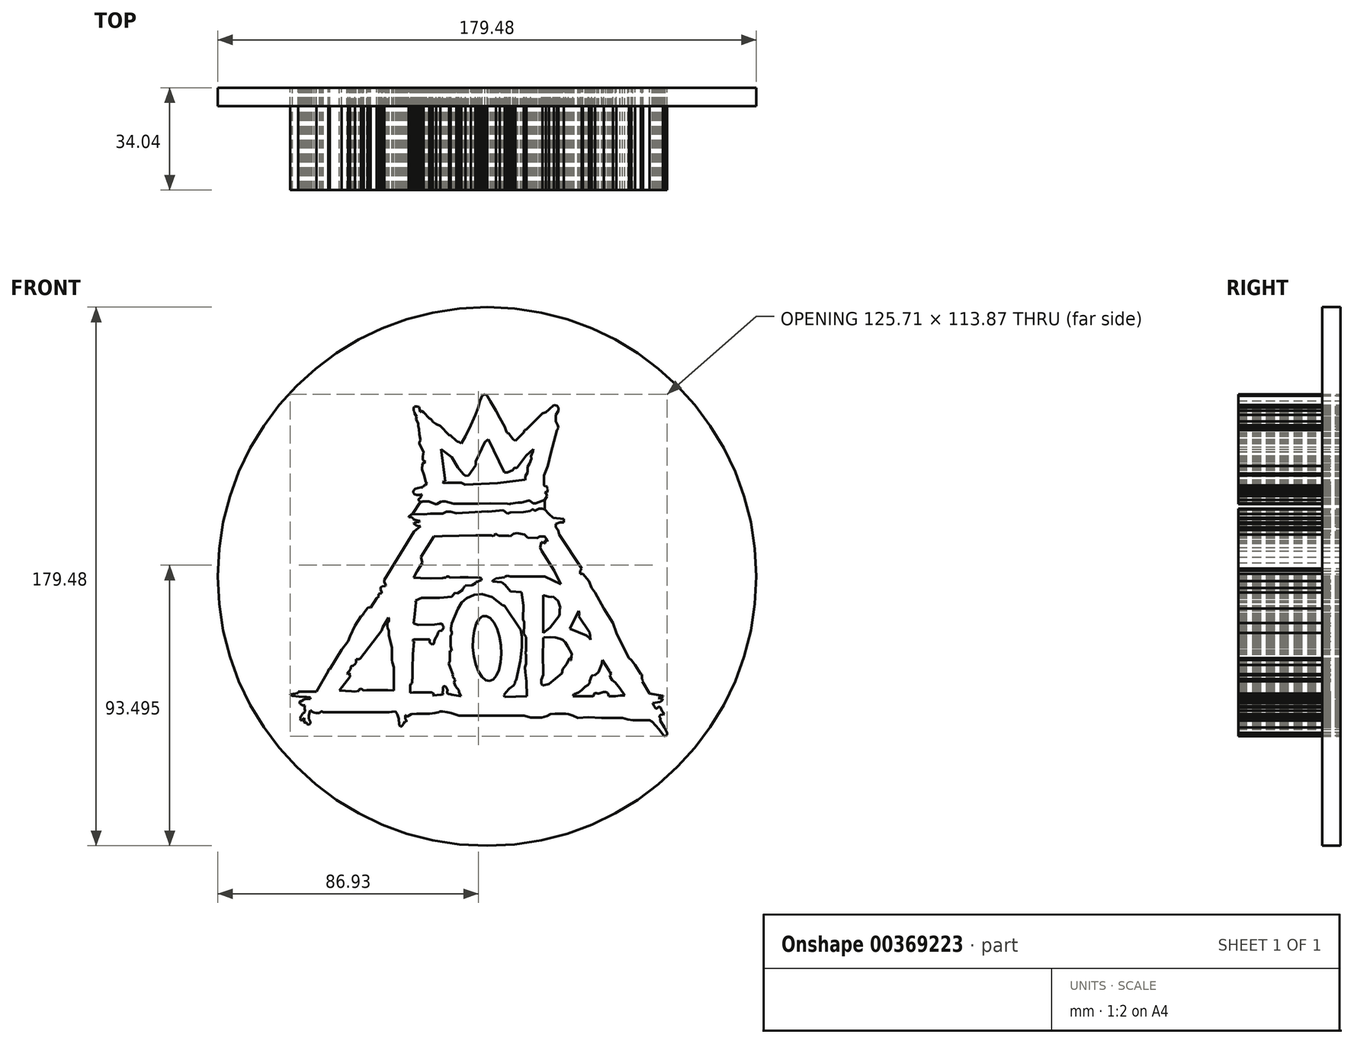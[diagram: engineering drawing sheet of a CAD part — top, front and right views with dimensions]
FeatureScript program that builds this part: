
annotation { "Feature Type Name" : "Feature", "Feature Type Description" : "" }
export const myFeature = defineFeature(function(context is Context, id is Id, definition is map)
    precondition{}
    {
        {
            var Q0;
            Q0=qCreatedBy(makeId("Front.planeOp"),FACE);
            var sketch = newSketch(context, id + "F0", { "sketchPlane" : qUnion([Q0])});
            skLineSegment(sketch, "E0", {"start": v(-62.94, -38.4) * mm, "end": v(-62.94, -38.9) * mm});
            skLineSegment(sketch, "E1", {"start": v(-62.94, -38.9) * mm, "end": v(-65.66, -39.21) * mm});
            skLineSegment(sketch, "E2", {"start": v(-65.66, -39.21) * mm, "end": v(-65.66, -39.45) * mm});
            skLineSegment(sketch, "E3", {"start": v(-65.66, -39.45) * mm, "end": v(-64.85, -39.72) * mm});
            skLineSegment(sketch, "E4", {"start": v(-64.85, -39.72) * mm, "end": v(-62.67, -39.97) * mm});
            skLineSegment(sketch, "E5", {"start": v(-62.67, -39.97) * mm, "end": v(-60.13, -40.15) * mm});
            skLineSegment(sketch, "E6", {"start": v(-60.13, -40.15) * mm, "end": v(-59.1, -40.28) * mm});
            skLineSegment(sketch, "E7", {"start": v(-59.1, -40.28) * mm, "end": v(-58.84, -40.47) * mm});
            skLineSegment(sketch, "E8", {"start": v(-58.84, -40.47) * mm, "end": v(-58.84, -40.74) * mm});
            skLineSegment(sketch, "E9", {"start": v(-58.84, -40.74) * mm, "end": v(-59.6, -40.74) * mm});
            skLineSegment(sketch, "E10", {"start": v(-59.6, -40.74) * mm, "end": v(-60.49, -40.74) * mm});
            skLineSegment(sketch, "E11", {"start": v(-60.49, -40.74) * mm, "end": v(-61.46, -41.23) * mm});
            skLineSegment(sketch, "E12", {"start": v(-61.46, -41.23) * mm, "end": v(-61.58, -41.33) * mm});
            skLineSegment(sketch, "E13", {"start": v(-61.58, -41.33) * mm, "end": v(-61.58, -41.7) * mm});
            skLineSegment(sketch, "E14", {"start": v(-61.58, -41.7) * mm, "end": v(-61.93, -41.55) * mm});
            skLineSegment(sketch, "E15", {"start": v(-61.93, -41.55) * mm, "end": v(-62.35, -41.55) * mm});
            skLineSegment(sketch, "E16", {"start": v(-62.35, -41.55) * mm, "end": v(-62.46, -41.71) * mm});
            skLineSegment(sketch, "E17", {"start": v(-62.46, -41.71) * mm, "end": v(-62.46, -42.04) * mm});
            skLineSegment(sketch, "E18", {"start": v(-62.46, -42.04) * mm, "end": v(-62.35, -42.44) * mm});
            skLineSegment(sketch, "E19", {"start": v(-62.35, -42.44) * mm, "end": v(-61.46, -42.92) * mm});
            skLineSegment(sketch, "E20", {"start": v(-61.46, -42.92) * mm, "end": v(-60.65, -42.92) * mm});
            skLineSegment(sketch, "E21", {"start": v(-60.65, -42.92) * mm, "end": v(-60.75, -43.15) * mm});
            skLineSegment(sketch, "E22", {"start": v(-60.75, -43.15) * mm, "end": v(-60.83, -43.5) * mm});
            skLineSegment(sketch, "E23", {"start": v(-60.83, -43.5) * mm, "end": v(-60.83, -43.8) * mm});
            skLineSegment(sketch, "E24", {"start": v(-60.83, -43.8) * mm, "end": v(-60.72, -44.25) * mm});
            skLineSegment(sketch, "E25", {"start": v(-60.72, -44.25) * mm, "end": v(-60.6, -44.61) * mm});
            skLineSegment(sketch, "E26", {"start": v(-60.6, -44.61) * mm, "end": v(-60.6, -45.04) * mm});
            skLineSegment(sketch, "E27", {"start": v(-60.6, -45.04) * mm, "end": v(-60.94, -45.41) * mm});
            skLineSegment(sketch, "E28", {"start": v(-60.94, -45.41) * mm, "end": v(-61.39, -45.64) * mm});
            skLineSegment(sketch, "E29", {"start": v(-61.39, -45.64) * mm, "end": v(-61.52, -45.82) * mm});
            skLineSegment(sketch, "E30", {"start": v(-61.52, -45.82) * mm, "end": v(-61.6, -46) * mm});
            skLineSegment(sketch, "E31", {"start": v(-61.6, -46) * mm, "end": v(-61.65, -46.18) * mm});
            skLineSegment(sketch, "E32", {"start": v(-61.65, -46.18) * mm, "end": v(-61.81, -46.37) * mm});
            skLineSegment(sketch, "E33", {"start": v(-61.81, -46.37) * mm, "end": v(-62.03, -46.6) * mm});
            skLineSegment(sketch, "E34", {"start": v(-62.03, -46.6) * mm, "end": v(-62.14, -46.84) * mm});
            skLineSegment(sketch, "E35", {"start": v(-62.14, -46.84) * mm, "end": v(-62.14, -47.19) * mm});
            skLineSegment(sketch, "E36", {"start": v(-62.14, -47.19) * mm, "end": v(-62.03, -47.35) * mm});
            skLineSegment(sketch, "E37", {"start": v(-62.03, -47.35) * mm, "end": v(-62.14, -47.67) * mm});
            skLineSegment(sketch, "E38", {"start": v(-62.14, -47.67) * mm, "end": v(-62.14, -47.89) * mm});
            skLineSegment(sketch, "E39", {"start": v(-62.14, -47.89) * mm, "end": v(-61.9, -47.89) * mm});
            skLineSegment(sketch, "E40", {"start": v(-61.9, -47.89) * mm, "end": v(-61.39, -47.6) * mm});
            skLineSegment(sketch, "E41", {"start": v(-61.39, -47.6) * mm, "end": v(-60.97, -47.26) * mm});
            skLineSegment(sketch, "E42", {"start": v(-60.97, -47.26) * mm, "end": v(-60.85, -47.11) * mm});
            skLineSegment(sketch, "E43", {"start": v(-60.85, -47.11) * mm, "end": v(-60.85, -47.7) * mm});
            skLineSegment(sketch, "E44", {"start": v(-60.85, -47.7) * mm, "end": v(-60.98, -48.51) * mm});
            skLineSegment(sketch, "E45", {"start": v(-60.98, -48.51) * mm, "end": v(-60.74, -48.71) * mm});
            skLineSegment(sketch, "E46", {"start": v(-60.74, -48.71) * mm, "end": v(-60.44, -48.71) * mm});
            skLineSegment(sketch, "E47", {"start": v(-60.44, -48.71) * mm, "end": v(-60.44, -48.57) * mm});
            skLineSegment(sketch, "E48", {"start": v(-60.44, -48.57) * mm, "end": v(-60.32, -48.57) * mm});
            skLineSegment(sketch, "E49", {"start": v(-60.32, -48.57) * mm, "end": v(-60.01, -49.24) * mm});
            skLineSegment(sketch, "E50", {"start": v(-60.01, -49.24) * mm, "end": v(-59.44, -49.41) * mm});
            skLineSegment(sketch, "E51", {"start": v(-59.44, -49.41) * mm, "end": v(-59, -49.1) * mm});
            skLineSegment(sketch, "E52", {"start": v(-59, -49.1) * mm, "end": v(-58.85, -48.77) * mm});
            skLineSegment(sketch, "E53", {"start": v(-58.85, -48.77) * mm, "end": v(-58.85, -48.24) * mm});
            skLineSegment(sketch, "E54", {"start": v(-58.85, -48.24) * mm, "end": v(-59.08, -47.96) * mm});
            skLineSegment(sketch, "E55", {"start": v(-59.08, -47.96) * mm, "end": v(-59.35, -47.81) * mm});
            skLineSegment(sketch, "E56", {"start": v(-59.35, -47.81) * mm, "end": v(-59.48, -47.81) * mm});
            skLineSegment(sketch, "E57", {"start": v(-59.48, -47.81) * mm, "end": v(-59.24, -47.6) * mm});
            skLineSegment(sketch, "E58", {"start": v(-59.24, -47.6) * mm, "end": v(-59.35, -47.47) * mm});
            skLineSegment(sketch, "E59", {"start": v(-59.35, -47.47) * mm, "end": v(-59.35, -46.25) * mm});
            skLineSegment(sketch, "E60", {"start": v(-59.35, -46.25) * mm, "end": v(-59.06, -44.8) * mm});
            skLineSegment(sketch, "E61", {"start": v(-59.06, -44.8) * mm, "end": v(-58.85, -44.6) * mm});
            skLineSegment(sketch, "E62", {"start": v(-58.85, -44.6) * mm, "end": v(-58.63, -44.67) * mm});
            skLineSegment(sketch, "E63", {"start": v(-58.63, -44.67) * mm, "end": v(-58.51, -44.86) * mm});
            skLineSegment(sketch, "E64", {"start": v(-58.51, -44.86) * mm, "end": v(-58.2, -45.08) * mm});
            skLineSegment(sketch, "E65", {"start": v(-58.2, -45.08) * mm, "end": v(-57.6, -45.35) * mm});
            skLineSegment(sketch, "E66", {"start": v(-57.6, -45.35) * mm, "end": v(-56.98, -45.51) * mm});
            skLineSegment(sketch, "E67", {"start": v(-56.98, -45.51) * mm, "end": v(-55.88, -45.44) * mm});
            skLineSegment(sketch, "E68", {"start": v(-55.88, -45.44) * mm, "end": v(-55.28, -44.98) * mm});
            skLineSegment(sketch, "E69", {"start": v(-55.28, -44.98) * mm, "end": v(-55, -44.98) * mm});
            skLineSegment(sketch, "E70", {"start": v(-55, -44.98) * mm, "end": v(-54.58, -45.26) * mm});
            skLineSegment(sketch, "E71", {"start": v(-54.58, -45.26) * mm, "end": v(-53.2, -45.26) * mm});
            skLineSegment(sketch, "E72", {"start": v(-53.2, -45.26) * mm, "end": v(-42.52, -45.26) * mm});
            skLineSegment(sketch, "E73", {"start": v(-42.52, -45.26) * mm, "end": v(-41.83, -45.26) * mm});
            skLineSegment(sketch, "E74", {"start": v(-41.83, -45.26) * mm, "end": v(-38.86, -45.26) * mm});
            skLineSegment(sketch, "E75", {"start": v(-38.86, -45.26) * mm, "end": v(-33.5, -45.26) * mm});
            skLineSegment(sketch, "E76", {"start": v(-33.5, -45.26) * mm, "end": v(-32.63, -45.26) * mm});
            skLineSegment(sketch, "E77", {"start": v(-32.63, -45.26) * mm, "end": v(-31.71, -45.08) * mm});
            skLineSegment(sketch, "E78", {"start": v(-31.71, -45.08) * mm, "end": v(-31.05, -44.98) * mm});
            skLineSegment(sketch, "E79", {"start": v(-31.05, -44.98) * mm, "end": v(-30.44, -45.08) * mm});
            skLineSegment(sketch, "E80", {"start": v(-30.44, -45.08) * mm, "end": v(-29.9, -45.89) * mm});
            skLineSegment(sketch, "E81", {"start": v(-29.9, -45.89) * mm, "end": v(-29.4, -47.44) * mm});
            skLineSegment(sketch, "E82", {"start": v(-29.4, -47.44) * mm, "end": v(-29.22, -49.27) * mm});
            skLineSegment(sketch, "E83", {"start": v(-29.22, -49.27) * mm, "end": v(-28.87, -50.01) * mm});
            skLineSegment(sketch, "E84", {"start": v(-28.87, -50.01) * mm, "end": v(-28.5, -49.91) * mm});
            skLineSegment(sketch, "E85", {"start": v(-28.5, -49.91) * mm, "end": v(-28.17, -49.53) * mm});
            skLineSegment(sketch, "E86", {"start": v(-28.17, -49.53) * mm, "end": v(-27.91, -49.13) * mm});
            skLineSegment(sketch, "E87", {"start": v(-27.91, -49.13) * mm, "end": v(-27.4, -48.24) * mm});
            skLineSegment(sketch, "E88", {"start": v(-27.4, -48.24) * mm, "end": v(-27.1, -48.24) * mm});
            skLineSegment(sketch, "E89", {"start": v(-27.1, -48.24) * mm, "end": v(-26.93, -48.42) * mm});
            skLineSegment(sketch, "E90", {"start": v(-26.93, -48.42) * mm, "end": v(-26.93, -47.92) * mm});
            skLineSegment(sketch, "E91", {"start": v(-26.93, -47.92) * mm, "end": v(-27.27, -47.5) * mm});
            skLineSegment(sketch, "E92", {"start": v(-27.27, -47.5) * mm, "end": v(-27.27, -46.32) * mm});
            skLineSegment(sketch, "E93", {"start": v(-27.27, -46.32) * mm, "end": v(-27.09, -46.32) * mm});
            skLineSegment(sketch, "E94", {"start": v(-27.09, -46.32) * mm, "end": v(-26.73, -46.6) * mm});
            skLineSegment(sketch, "E95", {"start": v(-26.73, -46.6) * mm, "end": v(-26.48, -46.6) * mm});
            skLineSegment(sketch, "E96", {"start": v(-26.48, -46.6) * mm, "end": v(-25.24, -45.85) * mm});
            skLineSegment(sketch, "E97", {"start": v(-25.24, -45.85) * mm, "end": v(-23.42, -45.69) * mm});
            skLineSegment(sketch, "E98", {"start": v(-23.42, -45.69) * mm, "end": v(-19.14, -45.69) * mm});
            skLineSegment(sketch, "E99", {"start": v(-19.14, -45.69) * mm, "end": v(-17.32, -45.46) * mm});
            skLineSegment(sketch, "E100", {"start": v(-17.32, -45.46) * mm, "end": v(-16.12, -45.3) * mm});
            skLineSegment(sketch, "E101", {"start": v(-16.12, -45.3) * mm, "end": v(-15.95, -45.18) * mm});
            skLineSegment(sketch, "E102", {"start": v(-15.95, -45.18) * mm, "end": v(-15.87, -45.02) * mm});
            skLineSegment(sketch, "E103", {"start": v(-15.87, -45.02) * mm, "end": v(-14.84, -45.02) * mm});
            skLineSegment(sketch, "E104", {"start": v(-14.84, -45.02) * mm, "end": v(-13.3, -45.24) * mm});
            skLineSegment(sketch, "E105", {"start": v(-13.3, -45.24) * mm, "end": v(-11.96, -45.46) * mm});
            skLineSegment(sketch, "E106", {"start": v(-11.96, -45.46) * mm, "end": v(-9.28, -46.4) * mm});
            skLineSegment(sketch, "E107", {"start": v(-9.28, -46.4) * mm, "end": v(-2.03, -46.4) * mm});
            skLineSegment(sketch, "E108", {"start": v(-2.03, -46.4) * mm, "end": v(12.34, -46.4) * mm});
            skLineSegment(sketch, "E109", {"start": v(12.34, -46.4) * mm, "end": v(14.52, -47.04) * mm});
            skLineSegment(sketch, "E110", {"start": v(14.52, -47.04) * mm, "end": v(18.18, -47.04) * mm});
            skLineSegment(sketch, "E111", {"start": v(18.18, -47.04) * mm, "end": v(20, -46.46) * mm});
            skLineSegment(sketch, "E112", {"start": v(20, -46.46) * mm, "end": v(21.2, -45.92) * mm});
            skLineSegment(sketch, "E113", {"start": v(21.2, -45.92) * mm, "end": v(22.7, -45.8) * mm});
            skLineSegment(sketch, "E114", {"start": v(22.7, -45.8) * mm, "end": v(26.26, -45.8) * mm});
            skLineSegment(sketch, "E115", {"start": v(26.26, -45.8) * mm, "end": v(27.11, -45.9) * mm});
            skLineSegment(sketch, "E116", {"start": v(27.11, -45.9) * mm, "end": v(28.61, -46.41) * mm});
            skLineSegment(sketch, "E117", {"start": v(28.61, -46.41) * mm, "end": v(30.22, -47.11) * mm});
            skLineSegment(sketch, "E118", {"start": v(30.22, -47.11) * mm, "end": v(33.7, -46.91) * mm});
            skLineSegment(sketch, "E119", {"start": v(33.7, -46.91) * mm, "end": v(38.12, -47.15) * mm});
            skLineSegment(sketch, "E120", {"start": v(38.12, -47.15) * mm, "end": v(45.11, -47.15) * mm});
            skLineSegment(sketch, "E121", {"start": v(45.11, -47.15) * mm, "end": v(46.95, -47.7) * mm});
            skLineSegment(sketch, "E122", {"start": v(46.95, -47.7) * mm, "end": v(48.53, -47.9) * mm});
            skLineSegment(sketch, "E123", {"start": v(48.53, -47.9) * mm, "end": v(54.18, -47.9) * mm});
            skLineSegment(sketch, "E124", {"start": v(54.18, -47.9) * mm, "end": v(55.04, -48.36) * mm});
            skLineSegment(sketch, "E125", {"start": v(55.04, -48.36) * mm, "end": v(57.38, -50.9) * mm});
            skLineSegment(sketch, "E126", {"start": v(57.38, -50.9) * mm, "end": v(57.92, -51.84) * mm});
            skLineSegment(sketch, "E127", {"start": v(57.92, -51.84) * mm, "end": v(58.9, -52.94) * mm});
            skLineSegment(sketch, "E128", {"start": v(58.9, -52.94) * mm, "end": v(59.36, -53.18) * mm});
            skLineSegment(sketch, "E129", {"start": v(59.36, -53.18) * mm, "end": v(60.04, -52.8) * mm});
            skLineSegment(sketch, "E130", {"start": v(60.04, -52.8) * mm, "end": v(60.04, -52.11) * mm});
            skLineSegment(sketch, "E131", {"start": v(60.04, -52.11) * mm, "end": v(59.17, -50.3) * mm});
            skLineSegment(sketch, "E132", {"start": v(59.17, -50.3) * mm, "end": v(57.75, -48.03) * mm});
            skLineSegment(sketch, "E133", {"start": v(57.75, -48.03) * mm, "end": v(57.75, -47.62) * mm});
            skLineSegment(sketch, "E134", {"start": v(57.75, -47.62) * mm, "end": v(57.83, -47.43) * mm});
            skLineSegment(sketch, "E135", {"start": v(57.83, -47.43) * mm, "end": v(57.83, -47.3) * mm});
            skLineSegment(sketch, "E136", {"start": v(57.83, -47.3) * mm, "end": v(57.74, -47.16) * mm});
            skLineSegment(sketch, "E137", {"start": v(57.74, -47.16) * mm, "end": v(57.47, -46.86) * mm});
            skLineSegment(sketch, "E138", {"start": v(57.47, -46.86) * mm, "end": v(57.47, -46.52) * mm});
            skLineSegment(sketch, "E139", {"start": v(57.47, -46.52) * mm, "end": v(57.9, -46.13) * mm});
            skLineSegment(sketch, "E140", {"start": v(57.9, -46.13) * mm, "end": v(59.09, -45.92) * mm});
            skLineSegment(sketch, "E141", {"start": v(59.09, -45.92) * mm, "end": v(58.22, -44.78) * mm});
            skLineSegment(sketch, "E142", {"start": v(58.22, -44.78) * mm, "end": v(57.83, -43.73) * mm});
            skLineSegment(sketch, "E143", {"start": v(57.83, -43.73) * mm, "end": v(57.6, -43.49) * mm});
            skLineSegment(sketch, "E144", {"start": v(57.6, -43.49) * mm, "end": v(57.09, -43.49) * mm});
            skLineSegment(sketch, "E145", {"start": v(57.09, -43.49) * mm, "end": v(56.64, -44) * mm});
            skLineSegment(sketch, "E146", {"start": v(56.64, -44) * mm, "end": v(56.24, -44) * mm});
            skLineSegment(sketch, "E147", {"start": v(56.24, -44) * mm, "end": v(55.7, -43.15) * mm});
            skLineSegment(sketch, "E148", {"start": v(55.7, -43.15) * mm, "end": v(55.2, -42.16) * mm});
            skLineSegment(sketch, "E149", {"start": v(55.2, -42.16) * mm, "end": v(57.74, -41.85) * mm});
            skLineSegment(sketch, "E150", {"start": v(57.74, -41.85) * mm, "end": v(58.51, -41.14) * mm});
            skLineSegment(sketch, "E151", {"start": v(58.51, -41.14) * mm, "end": v(58.51, -40.76) * mm});
            skLineSegment(sketch, "E152", {"start": v(58.51, -40.76) * mm, "end": v(57.09, -40.55) * mm});
            skLineSegment(sketch, "E153", {"start": v(57.09, -40.55) * mm, "end": v(58.7, -40.06) * mm});
            skLineSegment(sketch, "E154", {"start": v(58.7, -40.06) * mm, "end": v(58.62, -39.83) * mm});
            skLineSegment(sketch, "E155", {"start": v(58.62, -39.83) * mm, "end": v(54.18, -39.01) * mm});
            skLineSegment(sketch, "E156", {"start": v(54.18, -39.01) * mm, "end": v(51.7, -34.97) * mm});
            skLineSegment(sketch, "E157", {"start": v(51.7, -34.97) * mm, "end": v(52.02, -34.68) * mm});
            skLineSegment(sketch, "E158", {"start": v(52.02, -34.68) * mm, "end": v(51.6, -34.22) * mm});
            skLineSegment(sketch, "E159", {"start": v(51.6, -34.22) * mm, "end": v(51.6, -32.89) * mm});
            skLineSegment(sketch, "E160", {"start": v(51.6, -32.89) * mm, "end": v(51.63, -32.62) * mm});
            skLineSegment(sketch, "E161", {"start": v(51.63, -32.62) * mm, "end": v(51.23, -32.56) * mm});
            skLineSegment(sketch, "E162", {"start": v(51.23, -32.56) * mm, "end": v(49.34, -29.48) * mm});
            skLineSegment(sketch, "E163", {"start": v(49.34, -29.48) * mm, "end": v(48.07, -27.83) * mm});
            skLineSegment(sketch, "E164", {"start": v(48.07, -27.83) * mm, "end": v(47.35, -27.22) * mm});
            skLineSegment(sketch, "E165", {"start": v(47.35, -27.22) * mm, "end": v(45.83, -24.27) * mm});
            skLineSegment(sketch, "E166", {"start": v(45.83, -24.27) * mm, "end": v(43.05, -18.86) * mm});
            skLineSegment(sketch, "E167", {"start": v(43.05, -18.86) * mm, "end": v(41.96, -15.47) * mm});
            skLineSegment(sketch, "E168", {"start": v(41.96, -15.47) * mm, "end": v(38.94, -10.75) * mm});
            skLineSegment(sketch, "E169", {"start": v(38.94, -10.75) * mm, "end": v(35.97, -5.36) * mm});
            skLineSegment(sketch, "E170", {"start": v(35.97, -5.36) * mm, "end": v(34.88, -3.8) * mm});
            skLineSegment(sketch, "E171", {"start": v(34.88, -3.8) * mm, "end": v(33.91, -1.5) * mm});
            skLineSegment(sketch, "E172", {"start": v(33.91, -1.5) * mm, "end": v(31.98, 0.87) * mm});
            skLineSegment(sketch, "E173", {"start": v(31.98, 0.87) * mm, "end": v(31, 0.87) * mm});
            skLineSegment(sketch, "E174", {"start": v(31, 0.87) * mm, "end": v(31, 1.84) * mm});
            skLineSegment(sketch, "E175", {"start": v(31, 1.84) * mm, "end": v(31.55, 2.62) * mm});
            skLineSegment(sketch, "E176", {"start": v(31.55, 2.62) * mm, "end": v(24.1, 13.9) * mm});
            skLineSegment(sketch, "E177", {"start": v(24.1, 13.9) * mm, "end": v(23.67, 15.48) * mm});
            skLineSegment(sketch, "E178", {"start": v(23.67, 15.48) * mm, "end": v(22.9, 16.38) * mm});
            skLineSegment(sketch, "E179", {"start": v(22.9, 16.38) * mm, "end": v(22.9, 17.5) * mm});
            skLineSegment(sketch, "E180", {"start": v(22.9, 17.5) * mm, "end": v(24.27, 17.96) * mm});
            skLineSegment(sketch, "E181", {"start": v(24.27, 17.96) * mm, "end": v(25.55, 17.96) * mm});
            skLineSegment(sketch, "E182", {"start": v(25.55, 17.96) * mm, "end": v(25.55, 19.2) * mm});
            skLineSegment(sketch, "E183", {"start": v(25.55, 19.2) * mm, "end": v(22.09, 19.6) * mm});
            skLineSegment(sketch, "E184", {"start": v(22.09, 19.6) * mm, "end": v(20.68, 20.83) * mm});
            skLineSegment(sketch, "E185", {"start": v(20.68, 20.83) * mm, "end": v(19.28, 22.3) * mm});
            skLineSegment(sketch, "E186", {"start": v(19.28, 22.3) * mm, "end": v(19.28, 25.47) * mm});
            skLineSegment(sketch, "E187", {"start": v(19.28, 25.47) * mm, "end": v(19.98, 26.78) * mm});
            skLineSegment(sketch, "E188", {"start": v(19.98, 26.78) * mm, "end": v(19.7, 27.5) * mm});
            skLineSegment(sketch, "E189", {"start": v(19.7, 27.5) * mm, "end": v(19.28, 28.02) * mm});
            skLineSegment(sketch, "E190", {"start": v(19.28, 28.02) * mm, "end": v(20.08, 28.02) * mm});
            skLineSegment(sketch, "E191", {"start": v(20.08, 28.02) * mm, "end": v(20.08, 28.54) * mm});
            skLineSegment(sketch, "E192", {"start": v(20.08, 28.54) * mm, "end": v(20.27, 29.04) * mm});
            skLineSegment(sketch, "E193", {"start": v(20.27, 29.04) * mm, "end": v(20.05, 29.41) * mm});
            skLineSegment(sketch, "E194", {"start": v(20.05, 29.41) * mm, "end": v(20.05, 29.94) * mm});
            skLineSegment(sketch, "E195", {"start": v(20.05, 29.94) * mm, "end": v(19.77, 30.1) * mm});
            skLineSegment(sketch, "E196", {"start": v(19.77, 30.1) * mm, "end": v(19.46, 29.97) * mm});
            skLineSegment(sketch, "E197", {"start": v(19.46, 29.97) * mm, "end": v(18.96, 30.36) * mm});
            skLineSegment(sketch, "E198", {"start": v(18.96, 30.36) * mm, "end": v(18.96, 33.61) * mm});
            skLineSegment(sketch, "E199", {"start": v(18.96, 33.61) * mm, "end": v(19.28, 34.22) * mm});
            skLineSegment(sketch, "E200", {"start": v(19.28, 34.22) * mm, "end": v(20.23, 36.8) * mm});
            skLineSegment(sketch, "E201", {"start": v(20.23, 36.8) * mm, "end": v(21.3, 41.11) * mm});
            skLineSegment(sketch, "E202", {"start": v(21.3, 41.11) * mm, "end": v(23.24, 48.75) * mm});
            skLineSegment(sketch, "E203", {"start": v(23.24, 48.75) * mm, "end": v(23.8, 49.56) * mm});
            skLineSegment(sketch, "E204", {"start": v(23.8, 49.56) * mm, "end": v(23.56, 50.43) * mm});
            skLineSegment(sketch, "E205", {"start": v(23.56, 50.43) * mm, "end": v(22.95, 51.61) * mm});
            skLineSegment(sketch, "E206", {"start": v(22.95, 51.61) * mm, "end": v(22.95, 52.8) * mm});
            skLineSegment(sketch, "E207", {"start": v(22.95, 52.8) * mm, "end": v(22.95, 53.8) * mm});
            skLineSegment(sketch, "E208", {"start": v(22.95, 53.8) * mm, "end": v(23.8, 55.25) * mm});
            skLineSegment(sketch, "E209", {"start": v(23.8, 55.25) * mm, "end": v(23.8, 56.26) * mm});
            skLineSegment(sketch, "E210", {"start": v(23.8, 56.26) * mm, "end": v(23.35, 56.9) * mm});
            skLineSegment(sketch, "E211", {"start": v(23.35, 56.9) * mm, "end": v(22.34, 57.15) * mm});
            skLineSegment(sketch, "E212", {"start": v(22.34, 57.15) * mm, "end": v(20.63, 55.58) * mm});
            skLineSegment(sketch, "E213", {"start": v(20.63, 55.58) * mm, "end": v(19.59, 54.74) * mm});
            skLineSegment(sketch, "E214", {"start": v(19.59, 54.74) * mm, "end": v(18.44, 54.28) * mm});
            skLineSegment(sketch, "E215", {"start": v(18.44, 54.28) * mm, "end": v(13.15, 49.04) * mm});
            skLineSegment(sketch, "E216", {"start": v(13.15, 49.04) * mm, "end": v(12.44, 48.76) * mm});
            skLineSegment(sketch, "E217", {"start": v(12.44, 48.76) * mm, "end": v(12.24, 47.99) * mm});
            skLineSegment(sketch, "E218", {"start": v(12.24, 47.99) * mm, "end": v(9.49, 45.13) * mm});
            skLineSegment(sketch, "E219", {"start": v(9.49, 45.13) * mm, "end": v(8.67, 45.64) * mm});
            skLineSegment(sketch, "E220", {"start": v(8.67, 45.64) * mm, "end": v(7.83, 46.78) * mm});
            skLineSegment(sketch, "E221", {"start": v(7.83, 46.78) * mm, "end": v(7.3, 47.65) * mm});
            skLineSegment(sketch, "E222", {"start": v(7.3, 47.65) * mm, "end": v(6.6, 47.82) * mm});
            skLineSegment(sketch, "E223", {"start": v(6.6, 47.82) * mm, "end": v(6.23, 48.76) * mm});
            skLineSegment(sketch, "E224", {"start": v(6.23, 48.76) * mm, "end": v(5.85, 49.88) * mm});
            skLineSegment(sketch, "E225", {"start": v(5.85, 49.88) * mm, "end": v(4.3, 52.8) * mm});
            skLineSegment(sketch, "E226", {"start": v(4.3, 52.8) * mm, "end": v(2.93, 55.27) * mm});
            skLineSegment(sketch, "E227", {"start": v(2.93, 55.27) * mm, "end": v(1.08, 58.39) * mm});
            skLineSegment(sketch, "E228", {"start": v(1.08, 58.39) * mm, "end": v(0, 60.22) * mm});
            skLineSegment(sketch, "E229", {"start": v(0, 60.22) * mm, "end": v(-0.65, 60.7) * mm});
            skLineSegment(sketch, "E230", {"start": v(-0.65, 60.7) * mm, "end": v(-1.55, 60.26) * mm});
            skLineSegment(sketch, "E231", {"start": v(-1.55, 60.26) * mm, "end": v(-2.37, 58.5) * mm});
            skLineSegment(sketch, "E232", {"start": v(-2.37, 58.5) * mm, "end": v(-2.99, 56.07) * mm});
            skLineSegment(sketch, "E233", {"start": v(-2.99, 56.07) * mm, "end": v(-3.89, 53.78) * mm});
            skLineSegment(sketch, "E234", {"start": v(-3.89, 53.78) * mm, "end": v(-5.4, 50.43) * mm});
            skLineSegment(sketch, "E235", {"start": v(-5.4, 50.43) * mm, "end": v(-7.2, 46.73) * mm});
            skLineSegment(sketch, "E236", {"start": v(-7.2, 46.73) * mm, "end": v(-8.54, 44.28) * mm});
            skLineSegment(sketch, "E237", {"start": v(-8.54, 44.28) * mm, "end": v(-9.32, 44.82) * mm});
            skLineSegment(sketch, "E238", {"start": v(-9.32, 44.82) * mm, "end": v(-9.86, 44.96) * mm});
            skLineSegment(sketch, "E239", {"start": v(-9.86, 44.96) * mm, "end": v(-10.23, 45.14) * mm});
            skLineSegment(sketch, "E240", {"start": v(-10.23, 45.14) * mm, "end": v(-12.18, 46.93) * mm});
            skLineSegment(sketch, "E241", {"start": v(-12.18, 46.93) * mm, "end": v(-12.58, 47.03) * mm});
            skLineSegment(sketch, "E242", {"start": v(-12.58, 47.03) * mm, "end": v(-15.61, 50.11) * mm});
            skLineSegment(sketch, "E243", {"start": v(-15.61, 50.11) * mm, "end": v(-17.02, 50.8) * mm});
            skLineSegment(sketch, "E244", {"start": v(-17.02, 50.8) * mm, "end": v(-18.11, 51.54) * mm});
            skLineSegment(sketch, "E245", {"start": v(-18.11, 51.54) * mm, "end": v(-18.35, 52.04) * mm});
            skLineSegment(sketch, "E246", {"start": v(-18.35, 52.04) * mm, "end": v(-18.67, 52.47) * mm});
            skLineSegment(sketch, "E247", {"start": v(-18.67, 52.47) * mm, "end": v(-19.21, 52.73) * mm});
            skLineSegment(sketch, "E248", {"start": v(-19.21, 52.73) * mm, "end": v(-21.14, 54.74) * mm});
            skLineSegment(sketch, "E249", {"start": v(-21.14, 54.74) * mm, "end": v(-21.76, 55.04) * mm});
            skLineSegment(sketch, "E250", {"start": v(-21.76, 55.04) * mm, "end": v(-22.02, 55.1) * mm});
            skLineSegment(sketch, "E251", {"start": v(-22.02, 55.1) * mm, "end": v(-22.02, 54.83) * mm});
            skLineSegment(sketch, "E252", {"start": v(-22.02, 54.83) * mm, "end": v(-22.25, 54.89) * mm});
            skLineSegment(sketch, "E253", {"start": v(-22.25, 54.89) * mm, "end": v(-22.52, 56.05) * mm});
            skLineSegment(sketch, "E254", {"start": v(-22.52, 56.05) * mm, "end": v(-22.74, 56.5) * mm});
            skLineSegment(sketch, "E255", {"start": v(-22.74, 56.5) * mm, "end": v(-23.36, 56.67) * mm});
            skLineSegment(sketch, "E256", {"start": v(-23.36, 56.67) * mm, "end": v(-24.23, 56.67) * mm});
            skLineSegment(sketch, "E257", {"start": v(-24.23, 56.67) * mm, "end": v(-24.48, 56.17) * mm});
            skLineSegment(sketch, "E258", {"start": v(-24.48, 56.17) * mm, "end": v(-24.48, 55.25) * mm});
            skLineSegment(sketch, "E259", {"start": v(-24.48, 55.25) * mm, "end": v(-24.23, 54.84) * mm});
            skLineSegment(sketch, "E260", {"start": v(-24.23, 54.84) * mm, "end": v(-24.23, 54.44) * mm});
            skLineSegment(sketch, "E261", {"start": v(-24.23, 54.44) * mm, "end": v(-23.46, 53.16) * mm});
            skLineSegment(sketch, "E262", {"start": v(-23.46, 53.16) * mm, "end": v(-23.7, 52.45) * mm});
            skLineSegment(sketch, "E263", {"start": v(-23.7, 52.45) * mm, "end": v(-22.98, 51) * mm});
            skLineSegment(sketch, "E264", {"start": v(-22.98, 51) * mm, "end": v(-22.98, 50.11) * mm});
            skLineSegment(sketch, "E265", {"start": v(-22.98, 50.11) * mm, "end": v(-22.67, 49.17) * mm});
            skLineSegment(sketch, "E266", {"start": v(-22.67, 49.17) * mm, "end": v(-22.5, 47.29) * mm});
            skLineSegment(sketch, "E267", {"start": v(-22.5, 47.29) * mm, "end": v(-22.22, 45.43) * mm});
            skLineSegment(sketch, "E268", {"start": v(-22.22, 45.43) * mm, "end": v(-22.5, 44.62) * mm});
            skLineSegment(sketch, "E269", {"start": v(-22.5, 44.62) * mm, "end": v(-22.5, 44.24) * mm});
            skLineSegment(sketch, "E270", {"start": v(-22.5, 44.24) * mm, "end": v(-21.99, 43.12) * mm});
            skLineSegment(sketch, "E271", {"start": v(-21.99, 43.12) * mm, "end": v(-21.12, 41.49) * mm});
            skLineSegment(sketch, "E272", {"start": v(-21.12, 41.49) * mm, "end": v(-21.39, 39.92) * mm});
            skLineSegment(sketch, "E273", {"start": v(-21.39, 39.92) * mm, "end": v(-21.39, 38.8) * mm});
            skLineSegment(sketch, "E274", {"start": v(-21.39, 38.8) * mm, "end": v(-20.57, 38.16) * mm});
            skLineSegment(sketch, "E275", {"start": v(-20.57, 38.16) * mm, "end": v(-21.5, 37.62) * mm});
            skLineSegment(sketch, "E276", {"start": v(-21.5, 37.62) * mm, "end": v(-21.67, 35.71) * mm});
            skLineSegment(sketch, "E277", {"start": v(-21.67, 35.71) * mm, "end": v(-20.98, 33.88) * mm});
            skLineSegment(sketch, "E278", {"start": v(-20.98, 33.88) * mm, "end": v(-20.43, 31.53) * mm});
            skLineSegment(sketch, "E279", {"start": v(-20.43, 31.53) * mm, "end": v(-20.34, 31.37) * mm});
            skLineSegment(sketch, "E280", {"start": v(-20.34, 31.37) * mm, "end": v(-20.1, 31.37) * mm});
            skLineSegment(sketch, "E281", {"start": v(-20.1, 31.37) * mm, "end": v(-20.1, 31.03) * mm});
            skLineSegment(sketch, "E282", {"start": v(-20.1, 31.03) * mm, "end": v(-20.55, 30.51) * mm});
            skLineSegment(sketch, "E283", {"start": v(-20.55, 30.51) * mm, "end": v(-20.95, 30.38) * mm});
            skLineSegment(sketch, "E284", {"start": v(-20.95, 30.38) * mm, "end": v(-21.33, 29.93) * mm});
            skLineSegment(sketch, "E285", {"start": v(-21.33, 29.93) * mm, "end": v(-21.47, 29.66) * mm});
            skLineSegment(sketch, "E286", {"start": v(-21.47, 29.66) * mm, "end": v(-21.9, 29.66) * mm});
            skLineSegment(sketch, "E287", {"start": v(-21.9, 29.66) * mm, "end": v(-23, 29.48) * mm});
            skLineSegment(sketch, "E288", {"start": v(-23, 29.48) * mm, "end": v(-23.9, 29.2) * mm});
            skLineSegment(sketch, "E289", {"start": v(-23.9, 29.2) * mm, "end": v(-24.37, 28.81) * mm});
            skLineSegment(sketch, "E290", {"start": v(-24.37, 28.81) * mm, "end": v(-24.64, 28.35) * mm});
            skLineSegment(sketch, "E291", {"start": v(-24.64, 28.35) * mm, "end": v(-24.64, 27.85) * mm});
            skLineSegment(sketch, "E292", {"start": v(-24.64, 27.85) * mm, "end": v(-24.18, 27.43) * mm});
            skLineSegment(sketch, "E293", {"start": v(-24.18, 27.43) * mm, "end": v(-23.38, 27.1) * mm});
            skLineSegment(sketch, "E294", {"start": v(-23.38, 27.1) * mm, "end": v(-22.3, 27.1) * mm});
            skLineSegment(sketch, "E295", {"start": v(-22.3, 27.1) * mm, "end": v(-22, 27.42) * mm});
            skLineSegment(sketch, "E296", {"start": v(-22, 27.42) * mm, "end": v(-21.84, 27.26) * mm});
            skLineSegment(sketch, "E297", {"start": v(-21.84, 27.26) * mm, "end": v(-21.84, 26.88) * mm});
            skLineSegment(sketch, "E298", {"start": v(-21.84, 26.88) * mm, "end": v(-22.3, 26.17) * mm});
            skLineSegment(sketch, "E299", {"start": v(-22.3, 26.17) * mm, "end": v(-22.8, 25.76) * mm});
            skLineSegment(sketch, "E300", {"start": v(-22.8, 25.76) * mm, "end": v(-22.8, 25.4) * mm});
            skLineSegment(sketch, "E301", {"start": v(-22.8, 25.4) * mm, "end": v(-22.2, 24.86) * mm});
            skLineSegment(sketch, "E302", {"start": v(-22.2, 24.86) * mm, "end": v(-24.79, 20.83) * mm});
            skLineSegment(sketch, "E303", {"start": v(-24.79, 20.83) * mm, "end": v(-25.37, 20.53) * mm});
            skLineSegment(sketch, "E304", {"start": v(-25.37, 20.53) * mm, "end": v(-26.12, 19.93) * mm});
            skLineSegment(sketch, "E305", {"start": v(-26.12, 19.93) * mm, "end": v(-26.12, 19.78) * mm});
            skLineSegment(sketch, "E306", {"start": v(-26.12, 19.78) * mm, "end": v(-24.92, 19.7) * mm});
            skLineSegment(sketch, "E307", {"start": v(-24.92, 19.7) * mm, "end": v(-24.7, 19.4) * mm});
            skLineSegment(sketch, "E308", {"start": v(-24.7, 19.4) * mm, "end": v(-24.59, 19.4) * mm});
            skLineSegment(sketch, "E309", {"start": v(-24.59, 19.4) * mm, "end": v(-24.59, 18.98) * mm});
            skLineSegment(sketch, "E310", {"start": v(-24.59, 18.98) * mm, "end": v(-23.64, 18.72) * mm});
            skLineSegment(sketch, "E311", {"start": v(-23.64, 18.72) * mm, "end": v(-22.53, 18.57) * mm});
            skLineSegment(sketch, "E312", {"start": v(-22.53, 18.57) * mm, "end": v(-22.4, 18.4) * mm});
            skLineSegment(sketch, "E313", {"start": v(-22.4, 18.4) * mm, "end": v(-22.56, 18.1) * mm});
            skLineSegment(sketch, "E314", {"start": v(-22.56, 18.1) * mm, "end": v(-24.28, 17.87) * mm});
            skLineSegment(sketch, "E315", {"start": v(-24.28, 17.87) * mm, "end": v(-24.42, 17.64) * mm});
            skLineSegment(sketch, "E316", {"start": v(-24.42, 17.64) * mm, "end": v(-23.5, 16.94) * mm});
            skLineSegment(sketch, "E317", {"start": v(-23.5, 16.94) * mm, "end": v(-22.67, 16.73) * mm});
            skLineSegment(sketch, "E318", {"start": v(-22.67, 16.73) * mm, "end": v(-22.16, 16.73) * mm});
            skLineSegment(sketch, "E319", {"start": v(-22.16, 16.73) * mm, "end": v(-24.35, 14.96) * mm});
            skLineSegment(sketch, "E320", {"start": v(-24.35, 14.96) * mm, "end": v(-34.27, -1.22) * mm});
            skLineSegment(sketch, "E321", {"start": v(-34.27, -1.22) * mm, "end": v(-34.27, -1.77) * mm});
            skLineSegment(sketch, "E322", {"start": v(-34.27, -1.77) * mm, "end": v(-33.7, -2.97) * mm});
            skLineSegment(sketch, "E323", {"start": v(-33.7, -2.97) * mm, "end": v(-33.84, -3.18) * mm});
            skLineSegment(sketch, "E324", {"start": v(-33.84, -3.18) * mm, "end": v(-34.94, -3.33) * mm});
            skLineSegment(sketch, "E325", {"start": v(-34.94, -3.33) * mm, "end": v(-35.36, -3.62) * mm});
            skLineSegment(sketch, "E326", {"start": v(-35.36, -3.62) * mm, "end": v(-35.5, -4.16) * mm});
            skLineSegment(sketch, "E327", {"start": v(-35.5, -4.16) * mm, "end": v(-35.11, -5.2) * mm});
            skLineSegment(sketch, "E328", {"start": v(-35.11, -5.2) * mm, "end": v(-35.06, -5.58) * mm});
            skLineSegment(sketch, "E329", {"start": v(-35.06, -5.58) * mm, "end": v(-35.9, -5.69) * mm});
            skLineSegment(sketch, "E330", {"start": v(-35.9, -5.69) * mm, "end": v(-36.19, -5.88) * mm});
            skLineSegment(sketch, "E331", {"start": v(-36.19, -5.88) * mm, "end": v(-36.19, -6.44) * mm});
            skLineSegment(sketch, "E332", {"start": v(-36.19, -6.44) * mm, "end": v(-35.95, -6.58) * mm});
            skLineSegment(sketch, "E333", {"start": v(-35.95, -6.58) * mm, "end": v(-36.8, -7.22) * mm});
            skLineSegment(sketch, "E334", {"start": v(-36.8, -7.22) * mm, "end": v(-37.48, -8.36) * mm});
            skLineSegment(sketch, "E335", {"start": v(-37.48, -8.36) * mm, "end": v(-38, -9.2) * mm});
            skLineSegment(sketch, "E336", {"start": v(-38, -9.2) * mm, "end": v(-38.78, -10.47) * mm});
            skLineSegment(sketch, "E337", {"start": v(-38.78, -10.47) * mm, "end": v(-39.26, -10.17) * mm});
            skLineSegment(sketch, "E338", {"start": v(-39.26, -10.17) * mm, "end": v(-39.76, -10.52) * mm});
            skLineSegment(sketch, "E339", {"start": v(-39.76, -10.52) * mm, "end": v(-41.07, -12.25) * mm});
            skLineSegment(sketch, "E340", {"start": v(-41.07, -12.25) * mm, "end": v(-41.5, -12.95) * mm});
            skLineSegment(sketch, "E341", {"start": v(-41.5, -12.95) * mm, "end": v(-42, -13.2) * mm});
            skLineSegment(sketch, "E342", {"start": v(-42, -13.2) * mm, "end": v(-43.96, -16.4) * mm});
            skLineSegment(sketch, "E343", {"start": v(-43.96, -16.4) * mm, "end": v(-45.67, -19.95) * mm});
            skLineSegment(sketch, "E344", {"start": v(-45.67, -19.95) * mm, "end": v(-46.33, -21.68) * mm});
            skLineSegment(sketch, "E345", {"start": v(-46.33, -21.68) * mm, "end": v(-48.48, -24.43) * mm});
            skLineSegment(sketch, "E346", {"start": v(-48.48, -24.43) * mm, "end": v(-49.43, -26) * mm});
            skLineSegment(sketch, "E347", {"start": v(-49.43, -26) * mm, "end": v(-50.06, -27.02) * mm});
            skLineSegment(sketch, "E348", {"start": v(-50.06, -27.02) * mm, "end": v(-52.45, -30.92) * mm});
            skLineSegment(sketch, "E349", {"start": v(-52.45, -30.92) * mm, "end": v(-52.85, -30.97) * mm});
            skLineSegment(sketch, "E350", {"start": v(-52.85, -30.97) * mm, "end": v(-52.85, -31.57) * mm});
            skLineSegment(sketch, "E351", {"start": v(-52.85, -31.57) * mm, "end": v(-56.78, -38.44) * mm});
            skLineSegment(sketch, "E352", {"start": v(-56.78, -38.44) * mm, "end": v(-62.94, -38.4) * mm});
            skLineSegment(sketch, "E353", {"start": v(-15.26, 42.35) * mm, "end": v(-13.93, 32.01) * mm});
            skLineSegment(sketch, "E354", {"start": v(-13.93, 32.01) * mm, "end": v(-13.9, 31.76) * mm});
            skLineSegment(sketch, "E355", {"start": v(-13.9, 31.76) * mm, "end": v(-14.76, 31.47) * mm});
            skLineSegment(sketch, "E356", {"start": v(-14.76, 31.47) * mm, "end": v(-14.47, 31.15) * mm});
            skLineSegment(sketch, "E357", {"start": v(-14.47, 31.15) * mm, "end": v(-13.2, 31.26) * mm});
            skLineSegment(sketch, "E358", {"start": v(-13.2, 31.26) * mm, "end": v(-11.49, 31.26) * mm});
            skLineSegment(sketch, "E359", {"start": v(-11.49, 31.26) * mm, "end": v(-8.6, 31.26) * mm});
            skLineSegment(sketch, "E360", {"start": v(-8.6, 31.26) * mm, "end": v(-7.3, 30.52) * mm});
            skLineSegment(sketch, "E361", {"start": v(-7.3, 30.52) * mm, "end": v(3.5, 31.03) * mm});
            skLineSegment(sketch, "E362", {"start": v(3.5, 31.03) * mm, "end": v(7.72, 31.58) * mm});
            skLineSegment(sketch, "E363", {"start": v(7.72, 31.58) * mm, "end": v(12.62, 32.21) * mm});
            skLineSegment(sketch, "E364", {"start": v(12.62, 32.21) * mm, "end": v(12.81, 32.1) * mm});
            skLineSegment(sketch, "E365", {"start": v(12.81, 32.1) * mm, "end": v(12.81, 33.39) * mm});
            skLineSegment(sketch, "E366", {"start": v(12.81, 33.39) * mm, "end": v(13.56, 34.6) * mm});
            skLineSegment(sketch, "E367", {"start": v(13.56, 34.6) * mm, "end": v(13.56, 36.5) * mm});
            skLineSegment(sketch, "E368", {"start": v(13.56, 36.5) * mm, "end": v(14.2, 37.54) * mm});
            skLineSegment(sketch, "E369", {"start": v(14.2, 37.54) * mm, "end": v(14.82, 39.25) * mm});
            skLineSegment(sketch, "E370", {"start": v(14.82, 39.25) * mm, "end": v(14.72, 40.06) * mm});
            skLineSegment(sketch, "E371", {"start": v(14.72, 40.06) * mm, "end": v(15.27, 41.67) * mm});
            skLineSegment(sketch, "E372", {"start": v(-22.2, 24.86) * mm, "end": v(-21.64, 24.86) * mm});
            skLineSegment(sketch, "E373", {"start": v(-21.64, 24.86) * mm, "end": v(-21.43, 25) * mm});
            skLineSegment(sketch, "E374", {"start": v(-21.43, 25) * mm, "end": v(-19.37, 25) * mm});
            skLineSegment(sketch, "E375", {"start": v(-19.37, 25) * mm, "end": v(-17.2, 24.15) * mm});
            skLineSegment(sketch, "E376", {"start": v(-17.2, 24.15) * mm, "end": v(-16.72, 24.15) * mm});
            skLineSegment(sketch, "E377", {"start": v(-16.72, 24.15) * mm, "end": v(-15.46, 24.86) * mm});
            skLineSegment(sketch, "E378", {"start": v(-15.46, 24.86) * mm, "end": v(-14.85, 25) * mm});
            skLineSegment(sketch, "E379", {"start": v(-14.85, 25) * mm, "end": v(-13.87, 25) * mm});
            skLineSegment(sketch, "E380", {"start": v(-13.87, 25) * mm, "end": v(-11.12, 24.24) * mm});
            skLineSegment(sketch, "E381", {"start": v(-11.12, 24.24) * mm, "end": v(-6.76, 24.24) * mm});
            skLineSegment(sketch, "E382", {"start": v(-6.76, 24.24) * mm, "end": v(-2.94, 24.24) * mm});
            skLineSegment(sketch, "E383", {"start": v(-2.94, 24.24) * mm, "end": v(1.02, 24.37) * mm});
            skLineSegment(sketch, "E384", {"start": v(1.02, 24.37) * mm, "end": v(6.74, 24.17) * mm});
            skLineSegment(sketch, "E385", {"start": v(6.74, 24.17) * mm, "end": v(7.52, 24.1) * mm});
            skLineSegment(sketch, "E386", {"start": v(7.52, 24.1) * mm, "end": v(7.82, 24.2) * mm});
            skLineSegment(sketch, "E387", {"start": v(7.82, 24.2) * mm, "end": v(10.37, 24.6) * mm});
            skLineSegment(sketch, "E388", {"start": v(10.37, 24.6) * mm, "end": v(11.5, 24.6) * mm});
            skLineSegment(sketch, "E389", {"start": v(11.5, 24.6) * mm, "end": v(13.83, 25.19) * mm});
            skLineSegment(sketch, "E390", {"start": v(13.83, 25.19) * mm, "end": v(14.27, 25.19) * mm});
            skLineSegment(sketch, "E391", {"start": v(14.27, 25.19) * mm, "end": v(15.29, 24.36) * mm});
            skLineSegment(sketch, "E392", {"start": v(15.29, 24.36) * mm, "end": v(16.17, 24.36) * mm});
            skLineSegment(sketch, "E393", {"start": v(16.17, 24.36) * mm, "end": v(19.28, 25.47) * mm});
            skLineSegment(sketch, "E394", {"start": v(19.28, 22.3) * mm, "end": v(18.37, 22.55) * mm});
            skLineSegment(sketch, "E395", {"start": v(18.37, 22.55) * mm, "end": v(17.4, 22.55) * mm});
            skLineSegment(sketch, "E396", {"start": v(17.4, 22.55) * mm, "end": v(16.08, 21.95) * mm});
            skLineSegment(sketch, "E397", {"start": v(16.08, 21.95) * mm, "end": v(15.8, 21.95) * mm});
            skLineSegment(sketch, "E398", {"start": v(15.8, 21.95) * mm, "end": v(15.4, 22.3) * mm});
            skLineSegment(sketch, "E399", {"start": v(15.4, 22.3) * mm, "end": v(15, 22.3) * mm});
            skLineSegment(sketch, "E400", {"start": v(15, 22.3) * mm, "end": v(14.42, 21.85) * mm});
            skLineSegment(sketch, "E401", {"start": v(14.42, 21.85) * mm, "end": v(12.1, 21.46) * mm});
            skLineSegment(sketch, "E402", {"start": v(12.1, 21.46) * mm, "end": v(7.82, 21.26) * mm});
            skLineSegment(sketch, "E403", {"start": v(7.82, 21.26) * mm, "end": v(6.74, 20.9) * mm});
            skLineSegment(sketch, "E404", {"start": v(6.74, 20.9) * mm, "end": v(5.4, 22.09) * mm});
            skLineSegment(sketch, "E405", {"start": v(5.4, 22.09) * mm, "end": v(0.36, 21.58) * mm});
            skLineSegment(sketch, "E406", {"start": v(0.36, 21.58) * mm, "end": v(0.25, 21.72) * mm});
            skLineSegment(sketch, "E407", {"start": v(0.25, 21.72) * mm, "end": v(-10.24, 21.08) * mm});
            skLineSegment(sketch, "E408", {"start": v(-10.24, 21.08) * mm, "end": v(-12.09, 21.51) * mm});
            skLineSegment(sketch, "E409", {"start": v(-12.09, 21.51) * mm, "end": v(-13.48, 21.51) * mm});
            skLineSegment(sketch, "E410", {"start": v(-13.48, 21.51) * mm, "end": v(-14.85, 20.98) * mm});
            skLineSegment(sketch, "E411", {"start": v(-14.85, 20.98) * mm, "end": v(-16.01, 20.89) * mm});
            skLineSegment(sketch, "E412", {"start": v(-16.01, 20.89) * mm, "end": v(-18.85, 20.89) * mm});
            skLineSegment(sketch, "E413", {"start": v(-18.85, 20.89) * mm, "end": v(-20.98, 20.7) * mm});
            skLineSegment(sketch, "E414", {"start": v(-20.98, 20.7) * mm, "end": v(-24.79, 20.83) * mm});
            skLineSegment(sketch, "E415", {"start": v(-15.26, 42.35) * mm, "end": v(-11.75, 39.77) * mm});
            skLineSegment(sketch, "E416", {"start": v(-11.75, 39.77) * mm, "end": v(-9.7, 36.35) * mm});
            skLineSegment(sketch, "E417", {"start": v(-9.7, 36.35) * mm, "end": v(-7.9, 34.1) * mm});
            skLineSegment(sketch, "E418", {"start": v(-7.9, 34.1) * mm, "end": v(-7.11, 33.56) * mm});
            skLineSegment(sketch, "E419", {"start": v(-7.11, 33.56) * mm, "end": v(-6.15, 33.68) * mm});
            skLineSegment(sketch, "E420", {"start": v(-6.15, 33.68) * mm, "end": v(-3.7, 37.06) * mm});
            skLineSegment(sketch, "E421", {"start": v(-3.7, 37.06) * mm, "end": v(-3.7, 38.35) * mm});
            skLineSegment(sketch, "E422", {"start": v(-3.7, 38.35) * mm, "end": v(-0.72, 44.74) * mm});
            skLineSegment(sketch, "E423", {"start": v(-0.72, 44.74) * mm, "end": v(0.42, 45.64) * mm});
            skLineSegment(sketch, "E424", {"start": v(0.42, 45.64) * mm, "end": v(5.8, 34.66) * mm});
            skLineSegment(sketch, "E425", {"start": v(5.8, 34.66) * mm, "end": v(6.74, 34.66) * mm});
            skLineSegment(sketch, "E426", {"start": v(6.74, 34.66) * mm, "end": v(8.59, 35.35) * mm});
            skLineSegment(sketch, "E427", {"start": v(8.59, 35.35) * mm, "end": v(9.03, 36.21) * mm});
            skLineSegment(sketch, "E428", {"start": v(9.03, 36.21) * mm, "end": v(9.92, 36.21) * mm});
            skLineSegment(sketch, "E429", {"start": v(9.92, 36.21) * mm, "end": v(13.03, 40.19) * mm});
            skLineSegment(sketch, "E430", {"start": v(13.03, 40.19) * mm, "end": v(15.4, 42.43) * mm});
            skLineSegment(sketch, "E431", {"start": v(15.4, 42.43) * mm, "end": v(15.27, 41.67) * mm});
            skLineSegment(sketch, "E432", {"start": v(-17.74, 13.26) * mm, "end": v(-14.93, 13.44) * mm});
            skLineSegment(sketch, "E433", {"start": v(-14.93, 13.44) * mm, "end": v(-3.71, 13.63) * mm});
            skLineSegment(sketch, "E434", {"start": v(-3.71, 13.63) * mm, "end": v(1.3, 13.63) * mm});
            skLineSegment(sketch, "E435", {"start": v(1.3, 13.63) * mm, "end": v(2.07, 13.43) * mm});
            skLineSegment(sketch, "E436", {"start": v(2.07, 13.43) * mm, "end": v(2.63, 13.78) * mm});
            skLineSegment(sketch, "E437", {"start": v(2.63, 13.78) * mm, "end": v(2.72, 14.34) * mm});
            skLineSegment(sketch, "E438", {"start": v(2.72, 14.34) * mm, "end": v(3.89, 13.52) * mm});
            skLineSegment(sketch, "E439", {"start": v(3.89, 13.52) * mm, "end": v(7.32, 13.52) * mm});
            skLineSegment(sketch, "E440", {"start": v(7.32, 13.52) * mm, "end": v(7.63, 13.35) * mm});
            skLineSegment(sketch, "E441", {"start": v(7.63, 13.35) * mm, "end": v(7.84, 13.46) * mm});
            skLineSegment(sketch, "E442", {"start": v(7.84, 13.46) * mm, "end": v(8.85, 14.2) * mm});
            skLineSegment(sketch, "E443", {"start": v(8.85, 14.2) * mm, "end": v(9.96, 14.47) * mm});
            skLineSegment(sketch, "E444", {"start": v(9.96, 14.47) * mm, "end": v(12.5, 14) * mm});
            skLineSegment(sketch, "E445", {"start": v(12.5, 14) * mm, "end": v(13.51, 12.98) * mm});
            skLineSegment(sketch, "E446", {"start": v(13.51, 12.98) * mm, "end": v(16.72, 12.81) * mm});
            skLineSegment(sketch, "E447", {"start": v(16.72, 12.81) * mm, "end": v(17.64, 13.26) * mm});
            skLineSegment(sketch, "E448", {"start": v(17.64, 13.26) * mm, "end": v(19.05, 13.26) * mm});
            skLineSegment(sketch, "E449", {"start": v(19.05, 13.26) * mm, "end": v(19.17, 13.45) * mm});
            skLineSegment(sketch, "E450", {"start": v(19.17, 13.45) * mm, "end": v(20.16, 12.1) * mm});
            skLineSegment(sketch, "E451", {"start": v(20.16, 12.1) * mm, "end": v(20.16, 11.61) * mm});
            skLineSegment(sketch, "E452", {"start": v(20.16, 11.61) * mm, "end": v(19.9, 11.87) * mm});
            skLineSegment(sketch, "E453", {"start": v(19.9, 11.87) * mm, "end": v(19.22, 11.87) * mm});
            skLineSegment(sketch, "E454", {"start": v(19.22, 11.87) * mm, "end": v(19.22, 11.63) * mm});
            skLineSegment(sketch, "E455", {"start": v(19.22, 11.63) * mm, "end": v(19.39, 11.29) * mm});
            skLineSegment(sketch, "E456", {"start": v(19.39, 11.29) * mm, "end": v(19.39, 10.96) * mm});
            skLineSegment(sketch, "E457", {"start": v(19.39, 10.96) * mm, "end": v(19.22, 10.96) * mm});
            skLineSegment(sketch, "E458", {"start": v(19.22, 10.96) * mm, "end": v(19.14, 11.1) * mm});
            skLineSegment(sketch, "E459", {"start": v(19.14, 11.1) * mm, "end": v(19.06, 11.18) * mm});
            skLineSegment(sketch, "E460", {"start": v(19.06, 11.18) * mm, "end": v(18.42, 11.22) * mm});
            skLineSegment(sketch, "E461", {"start": v(18.42, 11.22) * mm, "end": v(18.27, 11.35) * mm});
            skLineSegment(sketch, "E462", {"start": v(18.27, 11.35) * mm, "end": v(18.09, 11.35) * mm});
            skLineSegment(sketch, "E463", {"start": v(18.09, 11.35) * mm, "end": v(17.65, 9.57) * mm});
            skLineSegment(sketch, "E464", {"start": v(17.65, 9.57) * mm, "end": v(18.2, 8.46) * mm});
            skLineSegment(sketch, "E465", {"start": v(18.2, 8.46) * mm, "end": v(22.4, 1.82) * mm});
            skLineSegment(sketch, "E466", {"start": v(22.4, 1.82) * mm, "end": v(24.55, -2.55) * mm});
            skLineSegment(sketch, "E467", {"start": v(24.55, -2.55) * mm, "end": v(19.22, 0) * mm});
            skLineSegment(sketch, "E468", {"start": v(19.22, 0) * mm, "end": v(7.76, 0) * mm});
            skLineSegment(sketch, "E469", {"start": v(7.76, 0) * mm, "end": v(6.74, 0.25) * mm});
            skLineSegment(sketch, "E470", {"start": v(6.74, 0.25) * mm, "end": v(6.04, 0) * mm});
            skLineSegment(sketch, "E471", {"start": v(6.04, 0) * mm, "end": v(5.95, -0.26) * mm});
            skLineSegment(sketch, "E472", {"start": v(5.95, -0.26) * mm, "end": v(2.95, -0.7) * mm});
            skLineSegment(sketch, "E473", {"start": v(2.95, -0.7) * mm, "end": v(1.9, -1.47) * mm});
            skLineSegment(sketch, "E474", {"start": v(1.9, -1.47) * mm, "end": v(1.88, -1.64) * mm});
            skLineSegment(sketch, "E475", {"start": v(1.88, -1.64) * mm, "end": v(4.93, -1.9) * mm});
            skLineSegment(sketch, "E476", {"start": v(4.93, -1.9) * mm, "end": v(6.03, -2.8) * mm});
            skLineSegment(sketch, "E477", {"start": v(6.03, -2.8) * mm, "end": v(7.76, -5.04) * mm});
            skLineSegment(sketch, "E478", {"start": v(7.76, -5.04) * mm, "end": v(11.5, -5.25) * mm});
            skLineSegment(sketch, "E479", {"start": v(11.5, -5.25) * mm, "end": v(12.1, -9.62) * mm});
            skLineSegment(sketch, "E480", {"start": v(12.1, -9.62) * mm, "end": v(12, -14.07) * mm});
            skLineSegment(sketch, "E481", {"start": v(12, -14.07) * mm, "end": v(12, -14.4) * mm});
            skLineSegment(sketch, "E482", {"start": v(12, -14.4) * mm, "end": v(12.36, -15.12) * mm});
            skLineSegment(sketch, "E483", {"start": v(12.36, -15.12) * mm, "end": v(12.36, -16.15) * mm});
            skLineSegment(sketch, "E484", {"start": v(12.36, -16.15) * mm, "end": v(12.23, -18.8) * mm});
            skLineSegment(sketch, "E485", {"start": v(12.23, -18.8) * mm, "end": v(12.25, -19.06) * mm});
            skLineSegment(sketch, "E486", {"start": v(12.25, -19.06) * mm, "end": v(12.58, -19.59) * mm});
            skLineSegment(sketch, "E487", {"start": v(12.58, -19.59) * mm, "end": v(12.97, -20.2) * mm});
            skLineSegment(sketch, "E488", {"start": v(12.97, -20.2) * mm, "end": v(12.97, -22.33) * mm});
            skLineSegment(sketch, "E489", {"start": v(12.97, -22.33) * mm, "end": v(12.97, -25.01) * mm});
            skLineSegment(sketch, "E490", {"start": v(12.97, -25.01) * mm, "end": v(12.65, -25.4) * mm});
            skLineSegment(sketch, "E491", {"start": v(12.65, -25.4) * mm, "end": v(12.97, -25.96) * mm});
            skLineSegment(sketch, "E492", {"start": v(12.97, -25.96) * mm, "end": v(12.97, -29.16) * mm});
            skLineSegment(sketch, "E493", {"start": v(12.97, -29.16) * mm, "end": v(12.6, -30.3) * mm});
            skLineSegment(sketch, "E494", {"start": v(12.6, -30.3) * mm, "end": v(12.82, -31.93) * mm});
            skLineSegment(sketch, "E495", {"start": v(12.82, -31.93) * mm, "end": v(13.15, -34.92) * mm});
            skLineSegment(sketch, "E496", {"start": v(13.15, -34.92) * mm, "end": v(13.32, -39.85) * mm});
            skLineSegment(sketch, "E497", {"start": v(13.32, -39.85) * mm, "end": v(5.88, -40.12) * mm});
            skLineSegment(sketch, "E498", {"start": v(5.88, -40.12) * mm, "end": v(5.66, -39.52) * mm});
            skLineSegment(sketch, "E499", {"start": v(5.66, -39.52) * mm, "end": v(6.33, -38.6) * mm});
            skLineSegment(sketch, "E500", {"start": v(6.33, -38.6) * mm, "end": v(7.45, -37.37) * mm});
            skLineSegment(sketch, "E501", {"start": v(7.45, -37.37) * mm, "end": v(8.82, -36.4) * mm});
            skLineSegment(sketch, "E502", {"start": v(8.82, -36.4) * mm, "end": v(9.35, -35.53) * mm});
            skLineSegment(sketch, "E503", {"start": v(9.35, -35.53) * mm, "end": v(9.35, -35.02) * mm});
            skLineSegment(sketch, "E504", {"start": v(9.35, -35.02) * mm, "end": v(9.73, -34.62) * mm});
            skLineSegment(sketch, "E505", {"start": v(9.73, -34.62) * mm, "end": v(11.14, -28.16) * mm});
            skLineSegment(sketch, "E506", {"start": v(11.14, -28.16) * mm, "end": v(11.65, -23.58) * mm});
            skLineSegment(sketch, "E507", {"start": v(11.65, -23.58) * mm, "end": v(11.65, -19.98) * mm});
            skLineSegment(sketch, "E508", {"start": v(11.65, -19.98) * mm, "end": v(11.18, -17.83) * mm});
            skLineSegment(sketch, "E509", {"start": v(11.18, -17.83) * mm, "end": v(5.78, -9.62) * mm});
            skLineSegment(sketch, "E510", {"start": v(5.78, -9.62) * mm, "end": v(5.3, -9.62) * mm});
            skLineSegment(sketch, "E511", {"start": v(5.3, -9.62) * mm, "end": v(1.69, -6.92) * mm});
            skLineSegment(sketch, "E512", {"start": v(1.69, -6.92) * mm, "end": v(-1.69, -5.82) * mm});
            skLineSegment(sketch, "E513", {"start": v(-1.69, -5.82) * mm, "end": v(-4.28, -6.17) * mm});
            skLineSegment(sketch, "E514", {"start": v(-4.28, -6.17) * mm, "end": v(-6.76, -7.23) * mm});
            skLineSegment(sketch, "E515", {"start": v(-6.76, -7.23) * mm, "end": v(-8.49, -8.6) * mm});
            skLineSegment(sketch, "E516", {"start": v(-8.49, -8.6) * mm, "end": v(-9.75, -10.8) * mm});
            skLineSegment(sketch, "E517", {"start": v(-9.75, -10.8) * mm, "end": v(-11.72, -15.7) * mm});
            skLineSegment(sketch, "E518", {"start": v(-11.72, -15.7) * mm, "end": v(-12.01, -17.28) * mm});
            skLineSegment(sketch, "E519", {"start": v(-12.01, -17.28) * mm, "end": v(-12.01, -17.91) * mm});
            skLineSegment(sketch, "E520", {"start": v(-12.01, -17.91) * mm, "end": v(-11.75, -18.54) * mm});
            skLineSegment(sketch, "E521", {"start": v(-11.75, -18.54) * mm, "end": v(-11.75, -19.3) * mm});
            skLineSegment(sketch, "E522", {"start": v(-11.75, -19.3) * mm, "end": v(-12.1, -19.7) * mm});
            skLineSegment(sketch, "E523", {"start": v(-12.1, -19.7) * mm, "end": v(-12.1, -23.2) * mm});
            skLineSegment(sketch, "E524", {"start": v(-12.1, -23.2) * mm, "end": v(-11.72, -24.75) * mm});
            skLineSegment(sketch, "E525", {"start": v(-11.72, -24.75) * mm, "end": v(-12.42, -24.75) * mm});
            skLineSegment(sketch, "E526", {"start": v(-12.42, -24.75) * mm, "end": v(-12.42, -28.19) * mm});
            skLineSegment(sketch, "E527", {"start": v(-12.42, -28.19) * mm, "end": v(-12.72, -29) * mm});
            skLineSegment(sketch, "E528", {"start": v(-12.72, -29) * mm, "end": v(-12.27, -30.34) * mm});
            skLineSegment(sketch, "E529", {"start": v(-12.27, -30.34) * mm, "end": v(-11.41, -32.73) * mm});
            skLineSegment(sketch, "E530", {"start": v(-11.41, -32.73) * mm, "end": v(-11.44, -33.3) * mm});
            skLineSegment(sketch, "E531", {"start": v(-11.44, -33.3) * mm, "end": v(-10.64, -34.45) * mm});
            skLineSegment(sketch, "E532", {"start": v(-10.64, -34.45) * mm, "end": v(-10.94, -35.31) * mm});
            skLineSegment(sketch, "E533", {"start": v(-10.94, -35.31) * mm, "end": v(-10.42, -36.65) * mm});
            skLineSegment(sketch, "E534", {"start": v(-10.42, -36.65) * mm, "end": v(-9.35, -38.05) * mm});
            skLineSegment(sketch, "E535", {"start": v(-9.35, -38.05) * mm, "end": v(-9.35, -38.55) * mm});
            skLineSegment(sketch, "E536", {"start": v(-9.35, -38.55) * mm, "end": v(-8.66, -39.9) * mm});
            skLineSegment(sketch, "E537", {"start": v(-8.66, -39.9) * mm, "end": v(-11.8, -39.45) * mm});
            skLineSegment(sketch, "E538", {"start": v(-11.8, -39.45) * mm, "end": v(-12.08, -39.3) * mm});
            skLineSegment(sketch, "E539", {"start": v(-12.08, -39.3) * mm, "end": v(-13.04, -39.2) * mm});
            skLineSegment(sketch, "E540", {"start": v(-13.04, -39.2) * mm, "end": v(-13.18, -39.05) * mm});
            skLineSegment(sketch, "E541", {"start": v(-13.18, -39.05) * mm, "end": v(-13.29, -38.65) * mm});
            skLineSegment(sketch, "E542", {"start": v(-13.29, -38.65) * mm, "end": v(-13.29, -38.3) * mm});
            skLineSegment(sketch, "E543", {"start": v(-13.29, -38.3) * mm, "end": v(-13.2, -37.99) * mm});
            skLineSegment(sketch, "E544", {"start": v(-13.2, -37.99) * mm, "end": v(-13.2, -37.83) * mm});
            skLineSegment(sketch, "E545", {"start": v(-13.2, -37.83) * mm, "end": v(-13.71, -36.81) * mm});
            skLineSegment(sketch, "E546", {"start": v(-13.71, -36.81) * mm, "end": v(-13.86, -36.65) * mm});
            skLineSegment(sketch, "E547", {"start": v(-13.86, -36.65) * mm, "end": v(-14.1, -36.57) * mm});
            skLineSegment(sketch, "E548", {"start": v(-14.1, -36.57) * mm, "end": v(-14.33, -36.57) * mm});
            skLineSegment(sketch, "E549", {"start": v(-14.33, -36.57) * mm, "end": v(-14.5, -36.67) * mm});
            skLineSegment(sketch, "E550", {"start": v(-14.5, -36.67) * mm, "end": v(-14.64, -36.85) * mm});
            skLineSegment(sketch, "E551", {"start": v(-14.64, -36.85) * mm, "end": v(-14.71, -37.06) * mm});
            skLineSegment(sketch, "E552", {"start": v(-14.71, -37.06) * mm, "end": v(-14.68, -37.28) * mm});
            skLineSegment(sketch, "E553", {"start": v(-14.68, -37.28) * mm, "end": v(-14.66, -37.47) * mm});
            skLineSegment(sketch, "E554", {"start": v(-14.66, -37.47) * mm, "end": v(-14.66, -38.3) * mm});
            skLineSegment(sketch, "E555", {"start": v(-14.66, -38.3) * mm, "end": v(-14.77, -38.36) * mm});
            skLineSegment(sketch, "E556", {"start": v(-14.77, -38.36) * mm, "end": v(-14.8, -38.48) * mm});
            skLineSegment(sketch, "E557", {"start": v(-14.8, -38.48) * mm, "end": v(-14.8, -38.79) * mm});
            skLineSegment(sketch, "E558", {"start": v(-14.8, -38.79) * mm, "end": v(-14.72, -38.85) * mm});
            skLineSegment(sketch, "E559", {"start": v(-14.72, -38.85) * mm, "end": v(-14.63, -38.88) * mm});
            skLineSegment(sketch, "E560", {"start": v(-14.63, -38.88) * mm, "end": v(-14.63, -39.28) * mm});
            skLineSegment(sketch, "E561", {"start": v(-14.63, -39.28) * mm, "end": v(-15.32, -39.43) * mm});
            skLineSegment(sketch, "E562", {"start": v(-15.32, -39.43) * mm, "end": v(-16.66, -39.53) * mm});
            skLineSegment(sketch, "E563", {"start": v(-16.66, -39.53) * mm, "end": v(-18.02, -39.71) * mm});
            skLineSegment(sketch, "E564", {"start": v(-18.02, -39.71) * mm, "end": v(-18.1, -39.68) * mm});
            skLineSegment(sketch, "E565", {"start": v(-18.1, -39.68) * mm, "end": v(-18.1, -39.6) * mm});
            skLineSegment(sketch, "E566", {"start": v(-18.1, -39.6) * mm, "end": v(-17.72, -39.36) * mm});
            skLineSegment(sketch, "E567", {"start": v(-17.72, -39.36) * mm, "end": v(-17.66, -39.32) * mm});
            skLineSegment(sketch, "E568", {"start": v(-17.66, -39.32) * mm, "end": v(-17.68, -39.15) * mm});
            skLineSegment(sketch, "E569", {"start": v(-17.68, -39.15) * mm, "end": v(-17.8, -38.98) * mm});
            skLineSegment(sketch, "E570", {"start": v(-17.8, -38.98) * mm, "end": v(-18.21, -38.75) * mm});
            skLineSegment(sketch, "E571", {"start": v(-18.21, -38.75) * mm, "end": v(-18.4, -38.69) * mm});
            skLineSegment(sketch, "E572", {"start": v(-18.4, -38.69) * mm, "end": v(-19.59, -38.61) * mm});
            skLineSegment(sketch, "E573", {"start": v(-19.59, -38.61) * mm, "end": v(-22.58, -38.61) * mm});
            skLineSegment(sketch, "E574", {"start": v(-22.58, -38.61) * mm, "end": v(-24.57, -38.7) * mm});
            skLineSegment(sketch, "E575", {"start": v(-24.57, -38.7) * mm, "end": v(-25.56, -38.75) * mm});
            skLineSegment(sketch, "E576", {"start": v(-25.56, -38.75) * mm, "end": v(-25.56, -36.56) * mm});
            skLineSegment(sketch, "E577", {"start": v(-25.56, -36.56) * mm, "end": v(-25.6, -36.35) * mm});
            skLineSegment(sketch, "E578", {"start": v(-25.6, -36.35) * mm, "end": v(-25.38, -35.7) * mm});
            skLineSegment(sketch, "E579", {"start": v(-25.38, -35.7) * mm, "end": v(-25, -35.65) * mm});
            skLineSegment(sketch, "E580", {"start": v(-25, -35.65) * mm, "end": v(-25, -34.45) * mm});
            skLineSegment(sketch, "E581", {"start": v(-25, -34.45) * mm, "end": v(-24.85, -33.98) * mm});
            skLineSegment(sketch, "E582", {"start": v(-24.85, -33.98) * mm, "end": v(-24.85, -31.62) * mm});
            skLineSegment(sketch, "E583", {"start": v(-24.85, -31.62) * mm, "end": v(-24.85, -29.75) * mm});
            skLineSegment(sketch, "E584", {"start": v(-24.85, -29.75) * mm, "end": v(-24.85, -29.11) * mm});
            skLineSegment(sketch, "E585", {"start": v(-24.85, -29.11) * mm, "end": v(-24.72, -27.63) * mm});
            skLineSegment(sketch, "E586", {"start": v(-24.72, -27.63) * mm, "end": v(-24.65, -26) * mm});
            skLineSegment(sketch, "E587", {"start": v(-24.65, -26) * mm, "end": v(-24.28, -21.6) * mm});
            skLineSegment(sketch, "E588", {"start": v(-24.28, -21.6) * mm, "end": v(-24.72, -21.46) * mm});
            skLineSegment(sketch, "E589", {"start": v(-24.72, -21.46) * mm, "end": v(-24.8, -21.27) * mm});
            skLineSegment(sketch, "E590", {"start": v(-24.8, -21.27) * mm, "end": v(-24.68, -21.14) * mm});
            skLineSegment(sketch, "E591", {"start": v(-24.68, -21.14) * mm, "end": v(-24.45, -21.05) * mm});
            skLineSegment(sketch, "E592", {"start": v(-24.45, -21.05) * mm, "end": v(-24.28, -20.95) * mm});
            skLineSegment(sketch, "E593", {"start": v(-24.28, -20.95) * mm, "end": v(-19.14, -20.95) * mm});
            skLineSegment(sketch, "E594", {"start": v(-19.14, -20.95) * mm, "end": v(-19.14, -21.84) * mm});
            skLineSegment(sketch, "E595", {"start": v(-19.14, -21.84) * mm, "end": v(-18.93, -22.16) * mm});
            skLineSegment(sketch, "E596", {"start": v(-18.93, -22.16) * mm, "end": v(-18.5, -22.52) * mm});
            skLineSegment(sketch, "E597", {"start": v(-18.5, -22.52) * mm, "end": v(-18.25, -22.74) * mm});
            skLineSegment(sketch, "E598", {"start": v(-18.25, -22.74) * mm, "end": v(-17.68, -22.36) * mm});
            skLineSegment(sketch, "E599", {"start": v(-17.68, -22.36) * mm, "end": v(-17.5, -21.13) * mm});
            skLineSegment(sketch, "E600", {"start": v(-17.5, -21.13) * mm, "end": v(-16.46, -19.37) * mm});
            skLineSegment(sketch, "E601", {"start": v(-16.46, -19.37) * mm, "end": v(-16.29, -18.64) * mm});
            skLineSegment(sketch, "E602", {"start": v(-16.29, -18.64) * mm, "end": v(-15.93, -18.18) * mm});
            skLineSegment(sketch, "E603", {"start": v(-15.93, -18.18) * mm, "end": v(-15.21, -18.09) * mm});
            skLineSegment(sketch, "E604", {"start": v(-15.21, -18.09) * mm, "end": v(-14.92, -17.9) * mm});
            skLineSegment(sketch, "E605", {"start": v(-14.92, -17.9) * mm, "end": v(-14.5, -17.23) * mm});
            skLineSegment(sketch, "E606", {"start": v(-14.5, -17.23) * mm, "end": v(-14.41, -16.93) * mm});
            skLineSegment(sketch, "E607", {"start": v(-14.41, -16.93) * mm, "end": v(-14.55, -16.69) * mm});
            skLineSegment(sketch, "E608", {"start": v(-14.55, -16.69) * mm, "end": v(-14.63, -16.55) * mm});
            skLineSegment(sketch, "E609", {"start": v(-14.63, -16.55) * mm, "end": v(-14.86, -16.47) * mm});
            skLineSegment(sketch, "E610", {"start": v(-14.86, -16.47) * mm, "end": v(-14.86, -16.31) * mm});
            skLineSegment(sketch, "E611", {"start": v(-14.86, -16.31) * mm, "end": v(-14.84, -16.06) * mm});
            skLineSegment(sketch, "E612", {"start": v(-14.84, -16.06) * mm, "end": v(-15, -15.84) * mm});
            skLineSegment(sketch, "E613", {"start": v(-15, -15.84) * mm, "end": v(-15.87, -15.76) * mm});
            skLineSegment(sketch, "E614", {"start": v(-15.87, -15.76) * mm, "end": v(-17.5, -15.98) * mm});
            skLineSegment(sketch, "E615", {"start": v(-17.5, -15.98) * mm, "end": v(-22.95, -16.18) * mm});
            skLineSegment(sketch, "E616", {"start": v(-22.95, -16.18) * mm, "end": v(-24.28, -15.74) * mm});
            skLineSegment(sketch, "E617", {"start": v(-24.28, -15.74) * mm, "end": v(-24.42, -15.7) * mm});
            skLineSegment(sketch, "E618", {"start": v(-24.42, -15.7) * mm, "end": v(-24.06, -12.42) * mm});
            skLineSegment(sketch, "E619", {"start": v(-24.06, -12.42) * mm, "end": v(-23.74, -8.6) * mm});
            skLineSegment(sketch, "E620", {"start": v(-23.74, -8.6) * mm, "end": v(-23.82, -8.02) * mm});
            skLineSegment(sketch, "E621", {"start": v(-23.82, -8.02) * mm, "end": v(-21.84, -7.08) * mm});
            skLineSegment(sketch, "E622", {"start": v(-21.84, -7.08) * mm, "end": v(-15.87, -7.08) * mm});
            skLineSegment(sketch, "E623", {"start": v(-15.87, -7.08) * mm, "end": v(-11.72, -6.72) * mm});
            skLineSegment(sketch, "E624", {"start": v(-11.72, -6.72) * mm, "end": v(-10.77, -5.5) * mm});
            skLineSegment(sketch, "E625", {"start": v(-10.77, -5.5) * mm, "end": v(-10.64, -5.52) * mm});
            skLineSegment(sketch, "E626", {"start": v(-10.64, -5.52) * mm, "end": v(-10.36, -5.54) * mm});
            skLineSegment(sketch, "E627", {"start": v(-10.36, -5.54) * mm, "end": v(-9.82, -5.59) * mm});
            skLineSegment(sketch, "E628", {"start": v(-9.82, -5.59) * mm, "end": v(-8.03, -4.41) * mm});
            skLineSegment(sketch, "E629", {"start": v(-8.03, -4.41) * mm, "end": v(-8.08, -4) * mm});
            skLineSegment(sketch, "E630", {"start": v(-8.08, -4) * mm, "end": v(-7.77, -3.8) * mm});
            skLineSegment(sketch, "E631", {"start": v(-7.77, -3.8) * mm, "end": v(-7.38, -3.3) * mm});
            skLineSegment(sketch, "E632", {"start": v(-7.38, -3.3) * mm, "end": v(-7.3, -3.07) * mm});
            skLineSegment(sketch, "E633", {"start": v(-7.3, -3.07) * mm, "end": v(-5.05, -2.9) * mm});
            skLineSegment(sketch, "E634", {"start": v(-5.05, -2.9) * mm, "end": v(-3.79, -2.2) * mm});
            skLineSegment(sketch, "E635", {"start": v(-3.79, -2.2) * mm, "end": v(-3.71, -1.82) * mm});
            skLineSegment(sketch, "E636", {"start": v(-3.71, -1.82) * mm, "end": v(-3.27, -1.76) * mm});
            skLineSegment(sketch, "E637", {"start": v(-3.27, -1.76) * mm, "end": v(-2.5, -1.38) * mm});
            skLineSegment(sketch, "E638", {"start": v(-2.5, -1.38) * mm, "end": v(-2.01, -1.31) * mm});
            skLineSegment(sketch, "E639", {"start": v(-2.01, -1.31) * mm, "end": v(-1.86, -0.92) * mm});
            skLineSegment(sketch, "E640", {"start": v(-1.86, -0.92) * mm, "end": v(-1.89, -0.7) * mm});
            skLineSegment(sketch, "E641", {"start": v(-1.89, -0.7) * mm, "end": v(-2.12, -0.52) * mm});
            skLineSegment(sketch, "E642", {"start": v(-2.12, -0.52) * mm, "end": v(-2.48, -0.4) * mm});
            skLineSegment(sketch, "E643", {"start": v(-2.48, -0.4) * mm, "end": v(-6.3, -0.28) * mm});
            skLineSegment(sketch, "E644", {"start": v(-6.3, -0.28) * mm, "end": v(-9.02, -0.28) * mm});
            skLineSegment(sketch, "E645", {"start": v(-9.02, -0.28) * mm, "end": v(-12.43, -0.47) * mm});
            skLineSegment(sketch, "E646", {"start": v(-12.43, -0.47) * mm, "end": v(-12.63, -0.16) * mm});
            skLineSegment(sketch, "E647", {"start": v(-12.63, -0.16) * mm, "end": v(-12.88, 0) * mm});
            skLineSegment(sketch, "E648", {"start": v(-12.88, 0) * mm, "end": v(-13.22, -0.03) * mm});
            skLineSegment(sketch, "E649", {"start": v(-13.22, -0.03) * mm, "end": v(-13.46, -0.19) * mm});
            skLineSegment(sketch, "E650", {"start": v(-13.46, -0.19) * mm, "end": v(-13.71, -0.4) * mm});
            skLineSegment(sketch, "E651", {"start": v(-13.71, -0.4) * mm, "end": v(-14.32, -0.37) * mm});
            skLineSegment(sketch, "E652", {"start": v(-14.32, -0.37) * mm, "end": v(-14.75, -0.52) * mm});
            skLineSegment(sketch, "E653", {"start": v(-14.75, -0.52) * mm, "end": v(-14.95, -0.54) * mm});
            skLineSegment(sketch, "E654", {"start": v(-14.95, -0.54) * mm, "end": v(-18.68, -0.7) * mm});
            skLineSegment(sketch, "E655", {"start": v(-18.68, -0.7) * mm, "end": v(-22.23, -0.54) * mm});
            skLineSegment(sketch, "E656", {"start": v(-22.23, -0.54) * mm, "end": v(-24.42, -0.36) * mm});
            skLineSegment(sketch, "E657", {"start": v(-24.42, -0.36) * mm, "end": v(-23.26, 1.74) * mm});
            skLineSegment(sketch, "E658", {"start": v(-23.26, 1.74) * mm, "end": v(-21.5, 4.5) * mm});
            skLineSegment(sketch, "E659", {"start": v(-21.5, 4.5) * mm, "end": v(-22.06, 6.5) * mm});
            skLineSegment(sketch, "E660", {"start": v(-22.06, 6.5) * mm, "end": v(-17.74, 13.26) * mm});
            skLineSegment(sketch, "E661", {"start": v(30.54, -11.43) * mm, "end": v(27.63, -17.45) * mm});
            skLineSegment(sketch, "E662", {"start": v(27.63, -17.45) * mm, "end": v(33.2, -19.7) * mm});
            skLineSegment(sketch, "E663", {"start": v(33.2, -19.7) * mm, "end": v(34.16, -20.6) * mm});
            skLineSegment(sketch, "E664", {"start": v(34.16, -20.6) * mm, "end": v(34.5, -21.14) * mm});
            skLineSegment(sketch, "E665", {"start": v(34.5, -21.14) * mm, "end": v(34.2, -18.76) * mm});
            skLineSegment(sketch, "E666", {"start": v(34.2, -18.76) * mm, "end": v(32.99, -16.93) * mm});
            skLineSegment(sketch, "E667", {"start": v(32.99, -16.93) * mm, "end": v(31.64, -14.89) * mm});
            skLineSegment(sketch, "E668", {"start": v(31.64, -14.89) * mm, "end": v(30.57, -13.26) * mm});
            skLineSegment(sketch, "E669", {"start": v(30.57, -13.26) * mm, "end": v(30.74, -12.42) * mm});
            skLineSegment(sketch, "E670", {"start": v(30.74, -12.42) * mm, "end": v(30.54, -11.43) * mm});
            skLineSegment(sketch, "E671", {"start": v(38.38, -27.82) * mm, "end": v(40.64, -31.34) * mm});
            skLineSegment(sketch, "E672", {"start": v(40.64, -31.34) * mm, "end": v(40.77, -31.93) * mm});
            skLineSegment(sketch, "E673", {"start": v(40.77, -31.93) * mm, "end": v(41.5, -32.29) * mm});
            skLineSegment(sketch, "E674", {"start": v(41.5, -32.29) * mm, "end": v(40.94, -32.96) * mm});
            skLineSegment(sketch, "E675", {"start": v(40.94, -32.96) * mm, "end": v(41.02, -33.56) * mm});
            skLineSegment(sketch, "E676", {"start": v(41.02, -33.56) * mm, "end": v(41.72, -34.62) * mm});
            skLineSegment(sketch, "E677", {"start": v(41.72, -34.62) * mm, "end": v(42.72, -35.31) * mm});
            skLineSegment(sketch, "E678", {"start": v(42.72, -35.31) * mm, "end": v(44.3, -37.26) * mm});
            skLineSegment(sketch, "E679", {"start": v(44.3, -37.26) * mm, "end": v(45.86, -39.64) * mm});
            skLineSegment(sketch, "E680", {"start": v(45.86, -39.64) * mm, "end": v(44.44, -39.64) * mm});
            skLineSegment(sketch, "E681", {"start": v(44.44, -39.64) * mm, "end": v(42.83, -39.9) * mm});
            skLineSegment(sketch, "E682", {"start": v(42.83, -39.9) * mm, "end": v(40.53, -39.9) * mm});
            skLineSegment(sketch, "E683", {"start": v(40.53, -39.9) * mm, "end": v(40.33, -39) * mm});
            skLineSegment(sketch, "E684", {"start": v(40.33, -39) * mm, "end": v(40.18, -38.79) * mm});
            skLineSegment(sketch, "E685", {"start": v(40.18, -38.79) * mm, "end": v(39.56, -38.57) * mm});
            skLineSegment(sketch, "E686", {"start": v(39.56, -38.57) * mm, "end": v(38.85, -38.57) * mm});
            skLineSegment(sketch, "E687", {"start": v(38.85, -38.57) * mm, "end": v(37.3, -39) * mm});
            skLineSegment(sketch, "E688", {"start": v(37.3, -39) * mm, "end": v(36.8, -39.01) * mm});
            skLineSegment(sketch, "E689", {"start": v(36.8, -39.01) * mm, "end": v(36.7, -38.92) * mm});
            skLineSegment(sketch, "E690", {"start": v(36.7, -38.92) * mm, "end": v(35.92, -38.92) * mm});
            skLineSegment(sketch, "E691", {"start": v(35.92, -38.92) * mm, "end": v(35.6, -39.15) * mm});
            skLineSegment(sketch, "E692", {"start": v(35.6, -39.15) * mm, "end": v(35.6, -39.64) * mm});
            skLineSegment(sketch, "E693", {"start": v(35.6, -39.64) * mm, "end": v(35.32, -39.94) * mm});
            skLineSegment(sketch, "E694", {"start": v(35.32, -39.94) * mm, "end": v(28.58, -39.94) * mm});
            skLineSegment(sketch, "E695", {"start": v(28.58, -39.94) * mm, "end": v(28.97, -39.3) * mm});
            skLineSegment(sketch, "E696", {"start": v(28.97, -39.3) * mm, "end": v(30.53, -38.6) * mm});
            skLineSegment(sketch, "E697", {"start": v(30.53, -38.6) * mm, "end": v(31.54, -37.85) * mm});
            skLineSegment(sketch, "E698", {"start": v(31.54, -37.85) * mm, "end": v(32.66, -36.73) * mm});
            skLineSegment(sketch, "E699", {"start": v(32.66, -36.73) * mm, "end": v(33.55, -36.26) * mm});
            skLineSegment(sketch, "E700", {"start": v(33.55, -36.26) * mm, "end": v(34.22, -35.5) * mm});
            skLineSegment(sketch, "E701", {"start": v(34.22, -35.5) * mm, "end": v(34.22, -34.78) * mm});
            skLineSegment(sketch, "E702", {"start": v(34.22, -34.78) * mm, "end": v(34.82, -33.17) * mm});
            skLineSegment(sketch, "E703", {"start": v(34.82, -33.17) * mm, "end": v(35.33, -32.78) * mm});
            skLineSegment(sketch, "E704", {"start": v(35.33, -32.78) * mm, "end": v(35.7, -33) * mm});
            skLineSegment(sketch, "E705", {"start": v(35.7, -33) * mm, "end": v(37.16, -31.91) * mm});
            skLineSegment(sketch, "E706", {"start": v(37.16, -31.91) * mm, "end": v(38.2, -29.3) * mm});
            skLineSegment(sketch, "E707", {"start": v(38.2, -29.3) * mm, "end": v(38.38, -27.82) * mm});
            skLineSegment(sketch, "E708", {"start": v(18.86, -20.34) * mm, "end": v(18.67, -20.8) * mm});
            skLineSegment(sketch, "E709", {"start": v(18.67, -20.8) * mm, "end": v(18.67, -22.33) * mm});
            skLineSegment(sketch, "E710", {"start": v(18.67, -22.33) * mm, "end": v(18.57, -25.45) * mm});
            skLineSegment(sketch, "E711", {"start": v(18.57, -25.45) * mm, "end": v(18.67, -32.73) * mm});
            skLineSegment(sketch, "E712", {"start": v(18.67, -32.73) * mm, "end": v(18.13, -34.42) * mm});
            skLineSegment(sketch, "E713", {"start": v(18.13, -34.42) * mm, "end": v(18.13, -35.58) * mm});
            skLineSegment(sketch, "E714", {"start": v(18.13, -35.58) * mm, "end": v(18.42, -36.4) * mm});
            skLineSegment(sketch, "E715", {"start": v(18.42, -36.4) * mm, "end": v(20.68, -35.78) * mm});
            skLineSegment(sketch, "E716", {"start": v(20.68, -35.78) * mm, "end": v(24.96, -32.29) * mm});
            skLineSegment(sketch, "E717", {"start": v(24.96, -32.29) * mm, "end": v(25.26, -30.84) * mm});
            skLineSegment(sketch, "E718", {"start": v(25.26, -30.84) * mm, "end": v(26.57, -29.13) * mm});
            skLineSegment(sketch, "E719", {"start": v(26.57, -29.13) * mm, "end": v(27.5, -27.26) * mm});
            skLineSegment(sketch, "E720", {"start": v(27.5, -27.26) * mm, "end": v(27.68, -27.15) * mm});
            skLineSegment(sketch, "E721", {"start": v(27.68, -27.15) * mm, "end": v(27.84, -27.2) * mm});
            skLineSegment(sketch, "E722", {"start": v(27.84, -27.2) * mm, "end": v(27.84, -27.91) * mm});
            skLineSegment(sketch, "E723", {"start": v(27.84, -27.91) * mm, "end": v(27.96, -27.94) * mm});
            skLineSegment(sketch, "E724", {"start": v(27.96, -27.94) * mm, "end": v(28.16, -26.7) * mm});
            skLineSegment(sketch, "E725", {"start": v(28.16, -26.7) * mm, "end": v(28.3, -25.82) * mm});
            skLineSegment(sketch, "E726", {"start": v(28.3, -25.82) * mm, "end": v(26.92, -23.29) * mm});
            skLineSegment(sketch, "E727", {"start": v(26.92, -23.29) * mm, "end": v(26.06, -22) * mm});
            skLineSegment(sketch, "E728", {"start": v(26.06, -22) * mm, "end": v(25.21, -21.14) * mm});
            skLineSegment(sketch, "E729", {"start": v(25.21, -21.14) * mm, "end": v(24.21, -20.74) * mm});
            skLineSegment(sketch, "E730", {"start": v(24.21, -20.74) * mm, "end": v(22.78, -20.41) * mm});
            skLineSegment(sketch, "E731", {"start": v(22.78, -20.41) * mm, "end": v(21, -20.2) * mm});
            skLineSegment(sketch, "E732", {"start": v(21, -20.2) * mm, "end": v(18.86, -20.34) * mm});
            skLineSegment(sketch, "E733", {"start": v(-32.85, -13.73) * mm, "end": v(-34.72, -16.93) * mm});
            skLineSegment(sketch, "E734", {"start": v(-34.72, -16.93) * mm, "end": v(-35.1, -18.12) * mm});
            skLineSegment(sketch, "E735", {"start": v(-35.1, -18.12) * mm, "end": v(-42.22, -27.36) * mm});
            skLineSegment(sketch, "E736", {"start": v(-42.22, -27.36) * mm, "end": v(-42.76, -27.55) * mm});
            skLineSegment(sketch, "E737", {"start": v(-42.76, -27.55) * mm, "end": v(-43.58, -27.58) * mm});
            skLineSegment(sketch, "E738", {"start": v(-43.58, -27.58) * mm, "end": v(-43.58, -28.69) * mm});
            skLineSegment(sketch, "E739", {"start": v(-43.58, -28.69) * mm, "end": v(-44.02, -29.22) * mm});
            skLineSegment(sketch, "E740", {"start": v(-44.02, -29.22) * mm, "end": v(-44.7, -29.74) * mm});
            skLineSegment(sketch, "E741", {"start": v(-44.7, -29.74) * mm, "end": v(-45.1, -29.83) * mm});
            skLineSegment(sketch, "E742", {"start": v(-45.1, -29.83) * mm, "end": v(-45.38, -30.15) * mm});
            skLineSegment(sketch, "E743", {"start": v(-45.38, -30.15) * mm, "end": v(-45.44, -30.31) * mm});
            skLineSegment(sketch, "E744", {"start": v(-45.44, -30.31) * mm, "end": v(-45.44, -30.8) * mm});
            skLineSegment(sketch, "E745", {"start": v(-45.44, -30.8) * mm, "end": v(-45.53, -30.82) * mm});
            skLineSegment(sketch, "E746", {"start": v(-45.53, -30.82) * mm, "end": v(-45.53, -30.97) * mm});
            skLineSegment(sketch, "E747", {"start": v(-45.53, -30.97) * mm, "end": v(-46.65, -32.44) * mm});
            skLineSegment(sketch, "E748", {"start": v(-46.65, -32.44) * mm, "end": v(-46.55, -32.52) * mm});
            skLineSegment(sketch, "E749", {"start": v(-46.55, -32.52) * mm, "end": v(-45.92, -32.1) * mm});
            skLineSegment(sketch, "E750", {"start": v(-45.92, -32.1) * mm, "end": v(-45.82, -32.13) * mm});
            skLineSegment(sketch, "E751", {"start": v(-45.82, -32.13) * mm, "end": v(-45.82, -32.8) * mm});
            skLineSegment(sketch, "E752", {"start": v(-45.82, -32.8) * mm, "end": v(-45.71, -33.02) * mm});
            skLineSegment(sketch, "E753", {"start": v(-45.71, -33.02) * mm, "end": v(-45.7, -33.38) * mm});
            skLineSegment(sketch, "E754", {"start": v(-45.7, -33.38) * mm, "end": v(-49.22, -37.97) * mm});
            skLineSegment(sketch, "E755", {"start": v(-49.22, -37.97) * mm, "end": v(-45.1, -38.24) * mm});
            skLineSegment(sketch, "E756", {"start": v(-45.1, -38.24) * mm, "end": v(-44.25, -38.36) * mm});
            skLineSegment(sketch, "E757", {"start": v(-44.25, -38.36) * mm, "end": v(-42.62, -38.08) * mm});
            skLineSegment(sketch, "E758", {"start": v(-42.62, -38.08) * mm, "end": v(-42.64, -37.67) * mm});
            skLineSegment(sketch, "E759", {"start": v(-42.64, -37.67) * mm, "end": v(-42.22, -37.4) * mm});
            skLineSegment(sketch, "E760", {"start": v(-42.22, -37.4) * mm, "end": v(-41.63, -37.59) * mm});
            skLineSegment(sketch, "E761", {"start": v(-41.63, -37.59) * mm, "end": v(-41.21, -37.95) * mm});
            skLineSegment(sketch, "E762", {"start": v(-41.21, -37.95) * mm, "end": v(-40.12, -37.85) * mm});
            skLineSegment(sketch, "E763", {"start": v(-40.12, -37.85) * mm, "end": v(-33.08, -37.85) * mm});
            skLineSegment(sketch, "E764", {"start": v(-33.08, -37.85) * mm, "end": v(-31.1, -38.02) * mm});
            skLineSegment(sketch, "E765", {"start": v(-31.1, -38.02) * mm, "end": v(-31.1, -30.2) * mm});
            skLineSegment(sketch, "E766", {"start": v(-31.1, -30.2) * mm, "end": v(-31.56, -28.64) * mm});
            skLineSegment(sketch, "E767", {"start": v(-31.56, -28.64) * mm, "end": v(-31.73, -27.81) * mm});
            skLineSegment(sketch, "E768", {"start": v(-31.73, -27.81) * mm, "end": v(-31.7, -23.77) * mm});
            skLineSegment(sketch, "E769", {"start": v(-31.7, -23.77) * mm, "end": v(-32.76, -19.56) * mm});
            skLineSegment(sketch, "E770", {"start": v(-32.76, -19.56) * mm, "end": v(-32.76, -18.12) * mm});
            skLineSegment(sketch, "E771", {"start": v(-32.76, -18.12) * mm, "end": v(-33.14, -17.33) * mm});
            skLineSegment(sketch, "E772", {"start": v(-33.14, -17.33) * mm, "end": v(-33.26, -16.52) * mm});
            skLineSegment(sketch, "E773", {"start": v(-33.26, -16.52) * mm, "end": v(-33.16, -15.6) * mm});
            skLineSegment(sketch, "E774", {"start": v(-33.16, -15.6) * mm, "end": v(-32.85, -15.15) * mm});
            skLineSegment(sketch, "E775", {"start": v(-32.85, -15.15) * mm, "end": v(-32.76, -14.84) * mm});
            skLineSegment(sketch, "E776", {"start": v(-32.76, -14.84) * mm, "end": v(-32.76, -14.07) * mm});
            skLineSegment(sketch, "E777", {"start": v(-32.76, -14.07) * mm, "end": v(-32.73, -13.86) * mm});
            skLineSegment(sketch, "E778", {"start": v(-32.73, -13.86) * mm, "end": v(-32.85, -13.73) * mm});
            skEllipse(sketch, "E779", {"center": v(0, -23.99) * mm, "majorRadius": 10.89 * mm, "minorRadius": 4.7 * mm, "majorAxis": v(0.08, -1)});
            skLineSegment(sketch, "E780", {"start": v(18.78, -6.3) * mm, "end": v(18.78, -18.79) * mm});
            skLineSegment(sketch, "E781", {"start": v(18.78, -18.79) * mm, "end": v(21.04, -17) * mm});
            skLineSegment(sketch, "E782", {"start": v(21.04, -17) * mm, "end": v(24.04, -13.1) * mm});
            skLineSegment(sketch, "E783", {"start": v(24.04, -13.1) * mm, "end": v(24.23, -12.45) * mm});
            skLineSegment(sketch, "E784", {"start": v(24.23, -12.45) * mm, "end": v(24.23, -10.9) * mm});
            skLineSegment(sketch, "E785", {"start": v(24.23, -10.9) * mm, "end": v(24.45, -10.4) * mm});
            skLineSegment(sketch, "E786", {"start": v(24.45, -10.4) * mm, "end": v(23.64, -8.14) * mm});
            skLineSegment(sketch, "E787", {"start": v(23.64, -8.14) * mm, "end": v(21.93, -6.68) * mm});
            skLineSegment(sketch, "E788", {"start": v(21.93, -6.68) * mm, "end": v(21.49, -6.86) * mm});
            skLineSegment(sketch, "E789", {"start": v(21.49, -6.86) * mm, "end": v(20.47, -6.75) * mm});
            skLineSegment(sketch, "E790", {"start": v(20.47, -6.75) * mm, "end": v(18.78, -6.3) * mm});
            skCircle(sketch, "E791", {"center": v(0, 0) * mm, "radius": 89.74 * mm});
            skSolve(sketch);
        }
        {
            var Q0;
            Q0=makeQuery(id+"F0.imprint","IMPRINT",FACE,{"disambiguationData":[TD([[makeQuery(id+"F0.imprint","IMPRINT",EDGE,{"derivedFrom":sQuery(id+"F0.wireOp",EDGE,"E187")}),1.0]])]});
            var Q1;
            Q1=makeQuery(id+"F0.imprint","IMPRINT",FACE,{"disambiguationData":[TD([[makeQuery(id+"F0.imprint","IMPRINT",EDGE,{"derivedFrom":sQuery(id+"F0.wireOp",EDGE,"E0")}),1.0]])]});
            extrude(context, id + "F1", {"entities" : qUnion([Q0, Q1]), "depth" : 34.04 * mm});
        }
        {
            var Q0;
            Q0=makeQuery(id+"F0.imprint","IMPRINT",FACE,{"disambiguationData":[TD([[makeQuery(id+"F0.imprint","IMPRINT",EDGE,{"derivedFrom":sQuery(id+"F0.wireOp",EDGE,"E0")}),-1.0]])]});
            extrude(context, id + "F2", {"entities" : qUnion([Q0]), "depth" : 6.1 * mm});
        }
    });
